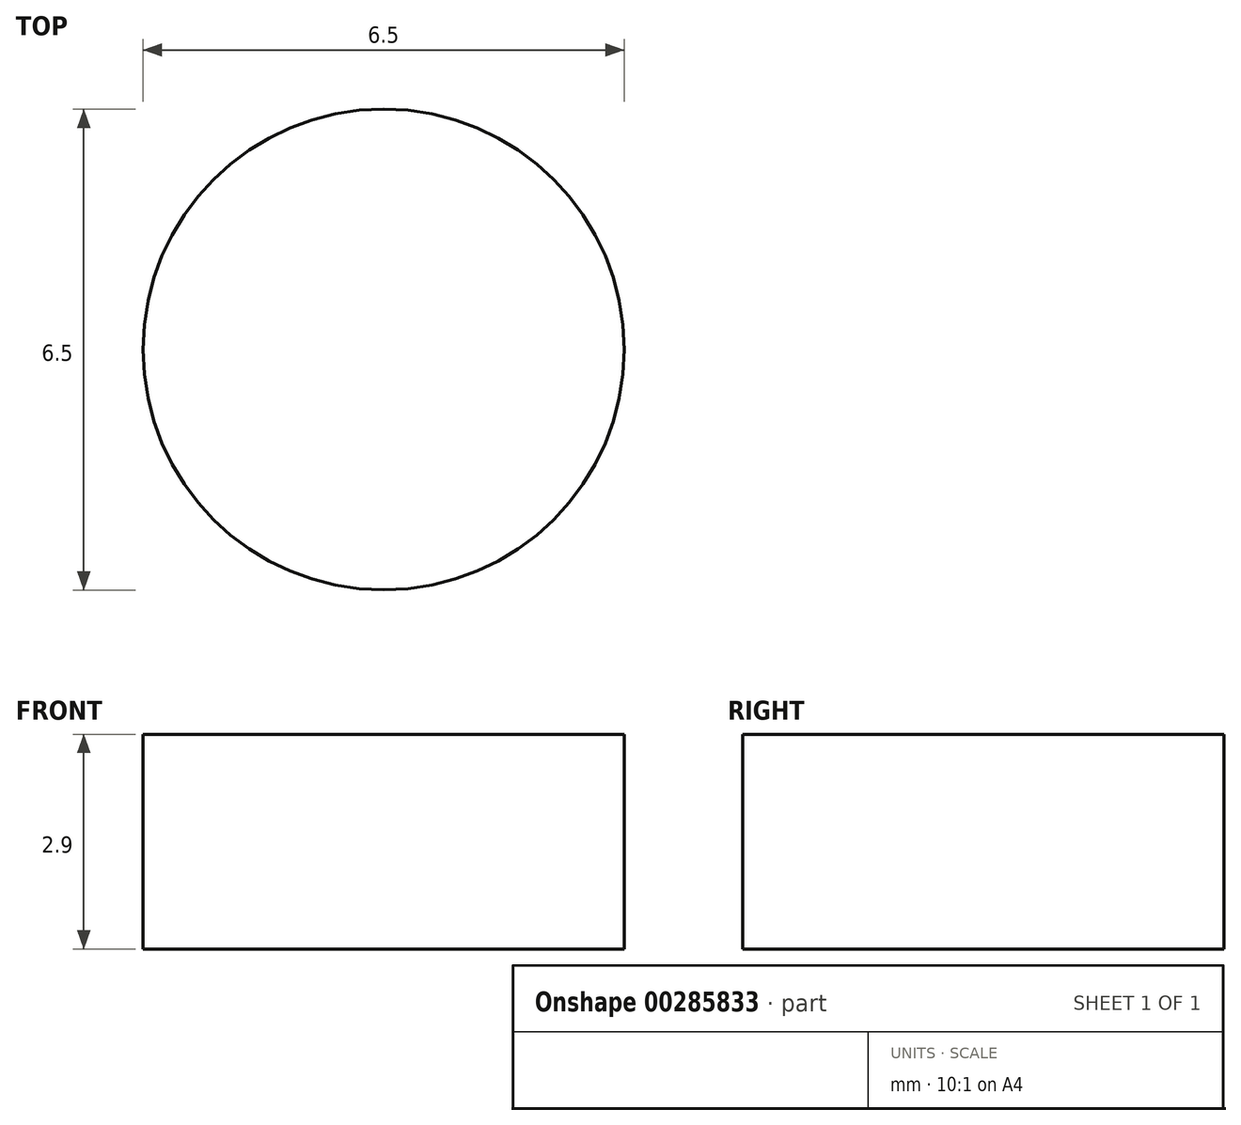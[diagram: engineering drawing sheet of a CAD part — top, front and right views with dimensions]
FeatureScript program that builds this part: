
annotation { "Feature Type Name" : "Feature", "Feature Type Description" : "" }
export const myFeature = defineFeature(function(context is Context, id is Id, definition is map)
    precondition{}
    {
        {
            var Q0;
            Q0=qCreatedBy(makeId("Top.planeOp"),FACE);
            var sketch = newSketch(context, id + "F0", { "sketchPlane" : qUnion([Q0])});
            skLineSegment(sketch, "E0", {"start": v(-29.75, -138) * mm, "end": v(-29.37, -138) * mm});
            skLineSegment(sketch, "E1", {"start": v(-29.37, -138) * mm, "end": v(-29.37, -133.46) * mm});
            skLineSegment(sketch, "E2", {"start": v(-29.37, -133.46) * mm, "end": v(-28.74, -138) * mm});
            skLineSegment(sketch, "E3", {"start": v(-28.74, -138) * mm, "end": v(-28.31, -138) * mm});
            skLineSegment(sketch, "E4", {"start": v(-28.31, -138) * mm, "end": v(-27.68, -133.46) * mm});
            skLineSegment(sketch, "E5", {"start": v(-27.68, -133.46) * mm, "end": v(-27.68, -138) * mm});
            skLineSegment(sketch, "E6", {"start": v(-27.68, -138) * mm, "end": v(-27.3, -138) * mm});
            skLineSegment(sketch, "E7", {"start": v(-27.3, -138) * mm, "end": v(-27.3, -133) * mm});
            skLineSegment(sketch, "E8", {"start": v(-27.3, -133) * mm, "end": v(-27.9, -133) * mm});
            skLineSegment(sketch, "E9", {"start": v(-27.9, -133) * mm, "end": v(-28.53, -137.4) * mm});
            skLineSegment(sketch, "E10", {"start": v(-28.53, -137.4) * mm, "end": v(-29.15, -133) * mm});
            skLineSegment(sketch, "E11", {"start": v(-29.15, -133) * mm, "end": v(-29.75, -133) * mm});
            skLineSegment(sketch, "E12", {"start": v(-29.75, -133) * mm, "end": v(-29.75, -138) * mm});
            skLineSegment(sketch, "E13", {"start": v(-24.53, -137.5) * mm, "end": v(-24.53, -137.51) * mm});
            skLineSegment(sketch, "E14", {"start": v(-24.53, -137.51) * mm, "end": v(-24.5, -137.76) * mm});
            skLineSegment(sketch, "E15", {"start": v(-24.5, -137.76) * mm, "end": v(-24.43, -137.93) * mm});
            skLineSegment(sketch, "E16", {"start": v(-24.43, -137.93) * mm, "end": v(-24.12, -138.07) * mm});
            skLineSegment(sketch, "E17", {"start": v(-24.12, -138.07) * mm, "end": v(-23.88, -138.01) * mm});
            skLineSegment(sketch, "E18", {"start": v(-23.88, -138.01) * mm, "end": v(-23.88, -137.52) * mm});
            skLineSegment(sketch, "E19", {"start": v(-23.88, -137.52) * mm, "end": v(-23.98, -137.54) * mm});
            skLineSegment(sketch, "E20", {"start": v(-23.98, -137.54) * mm, "end": v(-24.12, -137.45) * mm});
            skLineSegment(sketch, "E21", {"start": v(-24.12, -137.45) * mm, "end": v(-24.15, -137.16) * mm});
            skLineSegment(sketch, "E22", {"start": v(-24.15, -137.16) * mm, "end": v(-24.15, -135.16) * mm});
            skLineSegment(sketch, "E23", {"start": v(-24.15, -135.16) * mm, "end": v(-24.2, -134.65) * mm});
            skLineSegment(sketch, "E24", {"start": v(-24.2, -134.65) * mm, "end": v(-24.38, -134.29) * mm});
            skLineSegment(sketch, "E25", {"start": v(-24.38, -134.29) * mm, "end": v(-24.67, -134.07) * mm});
            skLineSegment(sketch, "E26", {"start": v(-24.67, -134.07) * mm, "end": v(-25.1, -133.99) * mm});
            skLineSegment(sketch, "E27", {"start": v(-25.1, -133.99) * mm, "end": v(-25.5, -134.08) * mm});
            skLineSegment(sketch, "E28", {"start": v(-25.5, -134.08) * mm, "end": v(-25.81, -134.32) * mm});
            skLineSegment(sketch, "E29", {"start": v(-25.81, -134.32) * mm, "end": v(-26, -134.7) * mm});
            skLineSegment(sketch, "E30", {"start": v(-26, -134.7) * mm, "end": v(-26.07, -135.2) * mm});
            skLineSegment(sketch, "E31", {"start": v(-26.07, -135.2) * mm, "end": v(-26.07, -135.25) * mm});
            skLineSegment(sketch, "E32", {"start": v(-26.07, -135.25) * mm, "end": v(-25.68, -135.25) * mm});
            skLineSegment(sketch, "E33", {"start": v(-25.68, -135.25) * mm, "end": v(-25.64, -134.95) * mm});
            skLineSegment(sketch, "E34", {"start": v(-25.64, -134.95) * mm, "end": v(-25.54, -134.73) * mm});
            skLineSegment(sketch, "E35", {"start": v(-25.54, -134.73) * mm, "end": v(-25.36, -134.6) * mm});
            skLineSegment(sketch, "E36", {"start": v(-25.36, -134.6) * mm, "end": v(-25.11, -134.55) * mm});
            skLineSegment(sketch, "E37", {"start": v(-25.11, -134.55) * mm, "end": v(-24.87, -134.59) * mm});
            skLineSegment(sketch, "E38", {"start": v(-24.87, -134.59) * mm, "end": v(-24.7, -134.7) * mm});
            skLineSegment(sketch, "E39", {"start": v(-24.7, -134.7) * mm, "end": v(-24.6, -134.88) * mm});
            skLineSegment(sketch, "E40", {"start": v(-24.6, -134.88) * mm, "end": v(-24.56, -135.14) * mm});
            skLineSegment(sketch, "E41", {"start": v(-24.56, -135.14) * mm, "end": v(-24.58, -135.45) * mm});
            skLineSegment(sketch, "E42", {"start": v(-24.58, -135.45) * mm, "end": v(-24.66, -135.6) * mm});
            skLineSegment(sketch, "E43", {"start": v(-24.66, -135.6) * mm, "end": v(-24.86, -135.67) * mm});
            skLineSegment(sketch, "E44", {"start": v(-24.86, -135.67) * mm, "end": v(-25.22, -135.73) * mm});
            skLineSegment(sketch, "E45", {"start": v(-25.22, -135.73) * mm, "end": v(-25.64, -135.86) * mm});
            skLineSegment(sketch, "E46", {"start": v(-25.64, -135.86) * mm, "end": v(-25.94, -136.09) * mm});
            skLineSegment(sketch, "E47", {"start": v(-25.94, -136.09) * mm, "end": v(-26.12, -136.45) * mm});
            skLineSegment(sketch, "E48", {"start": v(-26.12, -136.45) * mm, "end": v(-26.17, -136.98) * mm});
            skLineSegment(sketch, "E49", {"start": v(-26.17, -136.98) * mm, "end": v(-26.12, -137.46) * mm});
            skLineSegment(sketch, "E50", {"start": v(-26.12, -137.46) * mm, "end": v(-25.97, -137.8) * mm});
            skLineSegment(sketch, "E51", {"start": v(-25.97, -137.8) * mm, "end": v(-25.73, -138.03) * mm});
            skLineSegment(sketch, "E52", {"start": v(-25.73, -138.03) * mm, "end": v(-25.39, -138.11) * mm});
            skLineSegment(sketch, "E53", {"start": v(-25.39, -138.11) * mm, "end": v(-24.93, -137.96) * mm});
            skLineSegment(sketch, "E54", {"start": v(-24.93, -137.96) * mm, "end": v(-24.53, -137.5) * mm});
            skLineSegment(sketch, "E55", {"start": v(-24.58, -136.64) * mm, "end": v(-24.64, -137.02) * mm});
            skLineSegment(sketch, "E56", {"start": v(-24.64, -137.02) * mm, "end": v(-24.8, -137.3) * mm});
            skLineSegment(sketch, "E57", {"start": v(-24.8, -137.3) * mm, "end": v(-25.03, -137.5) * mm});
            skLineSegment(sketch, "E58", {"start": v(-25.03, -137.5) * mm, "end": v(-25.32, -137.56) * mm});
            skLineSegment(sketch, "E59", {"start": v(-25.32, -137.56) * mm, "end": v(-25.5, -137.52) * mm});
            skLineSegment(sketch, "E60", {"start": v(-25.5, -137.52) * mm, "end": v(-25.63, -137.4) * mm});
            skLineSegment(sketch, "E61", {"start": v(-25.63, -137.4) * mm, "end": v(-25.72, -137.2) * mm});
            skLineSegment(sketch, "E62", {"start": v(-25.72, -137.2) * mm, "end": v(-25.74, -136.92) * mm});
            skLineSegment(sketch, "E63", {"start": v(-25.74, -136.92) * mm, "end": v(-25.72, -136.67) * mm});
            skLineSegment(sketch, "E64", {"start": v(-25.72, -136.67) * mm, "end": v(-25.64, -136.49) * mm});
            skLineSegment(sketch, "E65", {"start": v(-25.64, -136.49) * mm, "end": v(-25.33, -136.29) * mm});
            skLineSegment(sketch, "E66", {"start": v(-25.33, -136.29) * mm, "end": v(-24.93, -136.2) * mm});
            skLineSegment(sketch, "E67", {"start": v(-24.93, -136.2) * mm, "end": v(-24.58, -136.03) * mm});
            skLineSegment(sketch, "E68", {"start": v(-24.58, -136.03) * mm, "end": v(-24.58, -136.64) * mm});
            skLineSegment(sketch, "E69", {"start": v(-22.61, -138) * mm, "end": v(-22.2, -138) * mm});
            skLineSegment(sketch, "E70", {"start": v(-22.2, -138) * mm, "end": v(-22.2, -134.4) * mm});
            skLineSegment(sketch, "E71", {"start": v(-22.2, -134.4) * mm, "end": v(-22.16, -133.92) * mm});
            skLineSegment(sketch, "E72", {"start": v(-22.16, -133.92) * mm, "end": v(-22.06, -133.57) * mm});
            skLineSegment(sketch, "E73", {"start": v(-22.06, -133.57) * mm, "end": v(-21.88, -133.37) * mm});
            skLineSegment(sketch, "E74", {"start": v(-21.88, -133.37) * mm, "end": v(-21.62, -133.3) * mm});
            skLineSegment(sketch, "E75", {"start": v(-21.62, -133.3) * mm, "end": v(-21.4, -133.36) * mm});
            skLineSegment(sketch, "E76", {"start": v(-21.4, -133.36) * mm, "end": v(-21.23, -133.52) * mm});
            skLineSegment(sketch, "E77", {"start": v(-21.23, -133.52) * mm, "end": v(-21.12, -133.77) * mm});
            skLineSegment(sketch, "E78", {"start": v(-21.12, -133.77) * mm, "end": v(-21.08, -134.1) * mm});
            skLineSegment(sketch, "E79", {"start": v(-21.08, -134.1) * mm, "end": v(-21.13, -134.47) * mm});
            skLineSegment(sketch, "E80", {"start": v(-21.13, -134.47) * mm, "end": v(-21.25, -134.72) * mm});
            skLineSegment(sketch, "E81", {"start": v(-21.25, -134.72) * mm, "end": v(-21.45, -134.88) * mm});
            skLineSegment(sketch, "E82", {"start": v(-21.45, -134.88) * mm, "end": v(-21.72, -134.93) * mm});
            skLineSegment(sketch, "E83", {"start": v(-21.72, -134.93) * mm, "end": v(-21.8, -134.93) * mm});
            skLineSegment(sketch, "E84", {"start": v(-21.8, -134.93) * mm, "end": v(-21.8, -135.45) * mm});
            skLineSegment(sketch, "E85", {"start": v(-21.8, -135.45) * mm, "end": v(-21.72, -135.45) * mm});
            skLineSegment(sketch, "E86", {"start": v(-21.72, -135.45) * mm, "end": v(-21.38, -135.52) * mm});
            skLineSegment(sketch, "E87", {"start": v(-21.38, -135.52) * mm, "end": v(-21.14, -135.7) * mm});
            skLineSegment(sketch, "E88", {"start": v(-21.14, -135.7) * mm, "end": v(-20.99, -136) * mm});
            skLineSegment(sketch, "E89", {"start": v(-20.99, -136) * mm, "end": v(-20.94, -136.43) * mm});
            skLineSegment(sketch, "E90", {"start": v(-20.94, -136.43) * mm, "end": v(-21, -136.9) * mm});
            skLineSegment(sketch, "E91", {"start": v(-21, -136.9) * mm, "end": v(-21.14, -137.23) * mm});
            skLineSegment(sketch, "E92", {"start": v(-21.14, -137.23) * mm, "end": v(-21.36, -137.45) * mm});
            skLineSegment(sketch, "E93", {"start": v(-21.36, -137.45) * mm, "end": v(-21.63, -137.52) * mm});
            skLineSegment(sketch, "E94", {"start": v(-21.63, -137.52) * mm, "end": v(-21.83, -137.48) * mm});
            skLineSegment(sketch, "E95", {"start": v(-21.83, -137.48) * mm, "end": v(-21.83, -138.07) * mm});
            skLineSegment(sketch, "E96", {"start": v(-21.83, -138.07) * mm, "end": v(-21.54, -138.12) * mm});
            skLineSegment(sketch, "E97", {"start": v(-21.54, -138.12) * mm, "end": v(-21.13, -138) * mm});
            skLineSegment(sketch, "E98", {"start": v(-21.13, -138) * mm, "end": v(-20.8, -137.64) * mm});
            skLineSegment(sketch, "E99", {"start": v(-20.8, -137.64) * mm, "end": v(-20.58, -137.09) * mm});
            skLineSegment(sketch, "E100", {"start": v(-20.58, -137.09) * mm, "end": v(-20.5, -136.36) * mm});
            skLineSegment(sketch, "E101", {"start": v(-20.5, -136.36) * mm, "end": v(-20.53, -135.94) * mm});
            skLineSegment(sketch, "E102", {"start": v(-20.53, -135.94) * mm, "end": v(-20.64, -135.57) * mm});
            skLineSegment(sketch, "E103", {"start": v(-20.64, -135.57) * mm, "end": v(-20.8, -135.29) * mm});
            skLineSegment(sketch, "E104", {"start": v(-20.8, -135.29) * mm, "end": v(-21.03, -135.1) * mm});
            skLineSegment(sketch, "E105", {"start": v(-21.03, -135.1) * mm, "end": v(-20.75, -134.71) * mm});
            skLineSegment(sketch, "E106", {"start": v(-20.75, -134.71) * mm, "end": v(-20.65, -134.05) * mm});
            skLineSegment(sketch, "E107", {"start": v(-20.65, -134.05) * mm, "end": v(-20.73, -133.52) * mm});
            skLineSegment(sketch, "E108", {"start": v(-20.73, -133.52) * mm, "end": v(-20.92, -133.1) * mm});
            skLineSegment(sketch, "E109", {"start": v(-20.92, -133.1) * mm, "end": v(-21.23, -132.84) * mm});
            skLineSegment(sketch, "E110", {"start": v(-21.23, -132.84) * mm, "end": v(-21.62, -132.74) * mm});
            skLineSegment(sketch, "E111", {"start": v(-21.62, -132.74) * mm, "end": v(-22.05, -132.84) * mm});
            skLineSegment(sketch, "E112", {"start": v(-22.05, -132.84) * mm, "end": v(-22.36, -133.14) * mm});
            skLineSegment(sketch, "E113", {"start": v(-22.36, -133.14) * mm, "end": v(-22.55, -133.63) * mm});
            skLineSegment(sketch, "E114", {"start": v(-22.55, -133.63) * mm, "end": v(-22.61, -134.3) * mm});
            skLineSegment(sketch, "E115", {"start": v(-22.61, -134.3) * mm, "end": v(-22.61, -138) * mm});
            skLineSegment(sketch, "E116", {"start": v(-17.9, -135.74) * mm, "end": v(-18.32, -135.6) * mm});
            skLineSegment(sketch, "E117", {"start": v(-18.32, -135.6) * mm, "end": v(-18.63, -135.43) * mm});
            skLineSegment(sketch, "E118", {"start": v(-18.63, -135.43) * mm, "end": v(-18.73, -135.1) * mm});
            skLineSegment(sketch, "E119", {"start": v(-18.73, -135.1) * mm, "end": v(-18.7, -134.85) * mm});
            skLineSegment(sketch, "E120", {"start": v(-18.7, -134.85) * mm, "end": v(-18.6, -134.68) * mm});
            skLineSegment(sketch, "E121", {"start": v(-18.6, -134.68) * mm, "end": v(-18.43, -134.57) * mm});
            skLineSegment(sketch, "E122", {"start": v(-18.43, -134.57) * mm, "end": v(-18.2, -134.53) * mm});
            skLineSegment(sketch, "E123", {"start": v(-18.2, -134.53) * mm, "end": v(-17.96, -134.57) * mm});
            skLineSegment(sketch, "E124", {"start": v(-17.96, -134.57) * mm, "end": v(-17.78, -134.7) * mm});
            skLineSegment(sketch, "E125", {"start": v(-17.78, -134.7) * mm, "end": v(-17.66, -134.9) * mm});
            skLineSegment(sketch, "E126", {"start": v(-17.66, -134.9) * mm, "end": v(-17.61, -135.16) * mm});
            skLineSegment(sketch, "E127", {"start": v(-17.61, -135.16) * mm, "end": v(-17.2, -135.16) * mm});
            skLineSegment(sketch, "E128", {"start": v(-17.2, -135.16) * mm, "end": v(-17.2, -135.14) * mm});
            skLineSegment(sketch, "E129", {"start": v(-17.2, -135.14) * mm, "end": v(-17.27, -134.67) * mm});
            skLineSegment(sketch, "E130", {"start": v(-17.27, -134.67) * mm, "end": v(-17.47, -134.3) * mm});
            skLineSegment(sketch, "E131", {"start": v(-17.47, -134.3) * mm, "end": v(-17.78, -134.08) * mm});
            skLineSegment(sketch, "E132", {"start": v(-17.78, -134.08) * mm, "end": v(-18.2, -133.99) * mm});
            skLineSegment(sketch, "E133", {"start": v(-18.2, -133.99) * mm, "end": v(-18.6, -134.08) * mm});
            skLineSegment(sketch, "E134", {"start": v(-18.6, -134.08) * mm, "end": v(-18.91, -134.31) * mm});
            skLineSegment(sketch, "E135", {"start": v(-18.91, -134.31) * mm, "end": v(-19.1, -134.67) * mm});
            skLineSegment(sketch, "E136", {"start": v(-19.1, -134.67) * mm, "end": v(-19.16, -135.11) * mm});
            skLineSegment(sketch, "E137", {"start": v(-19.16, -135.11) * mm, "end": v(-19.12, -135.55) * mm});
            skLineSegment(sketch, "E138", {"start": v(-19.12, -135.55) * mm, "end": v(-18.98, -135.85) * mm});
            skLineSegment(sketch, "E139", {"start": v(-18.98, -135.85) * mm, "end": v(-18.76, -136.06) * mm});
            skLineSegment(sketch, "E140", {"start": v(-18.76, -136.06) * mm, "end": v(-18.43, -136.22) * mm});
            skLineSegment(sketch, "E141", {"start": v(-18.43, -136.22) * mm, "end": v(-17.95, -136.39) * mm});
            skLineSegment(sketch, "E142", {"start": v(-17.95, -136.39) * mm, "end": v(-17.65, -136.57) * mm});
            skLineSegment(sketch, "E143", {"start": v(-17.65, -136.57) * mm, "end": v(-17.57, -136.71) * mm});
            skLineSegment(sketch, "E144", {"start": v(-17.57, -136.71) * mm, "end": v(-17.55, -136.93) * mm});
            skLineSegment(sketch, "E145", {"start": v(-17.55, -136.93) * mm, "end": v(-17.59, -137.2) * mm});
            skLineSegment(sketch, "E146", {"start": v(-17.59, -137.2) * mm, "end": v(-17.7, -137.4) * mm});
            skLineSegment(sketch, "E147", {"start": v(-17.7, -137.4) * mm, "end": v(-17.9, -137.53) * mm});
            skLineSegment(sketch, "E148", {"start": v(-17.9, -137.53) * mm, "end": v(-18.15, -137.57) * mm});
            skLineSegment(sketch, "E149", {"start": v(-18.15, -137.57) * mm, "end": v(-18.42, -137.53) * mm});
            skLineSegment(sketch, "E150", {"start": v(-18.42, -137.53) * mm, "end": v(-18.62, -137.38) * mm});
            skLineSegment(sketch, "E151", {"start": v(-18.62, -137.38) * mm, "end": v(-18.75, -137.13) * mm});
            skLineSegment(sketch, "E152", {"start": v(-18.75, -137.13) * mm, "end": v(-18.8, -136.8) * mm});
            skLineSegment(sketch, "E153", {"start": v(-18.8, -136.8) * mm, "end": v(-19.22, -136.8) * mm});
            skLineSegment(sketch, "E154", {"start": v(-19.22, -136.8) * mm, "end": v(-19.15, -137.37) * mm});
            skLineSegment(sketch, "E155", {"start": v(-19.15, -137.37) * mm, "end": v(-18.95, -137.79) * mm});
            skLineSegment(sketch, "E156", {"start": v(-18.95, -137.79) * mm, "end": v(-18.63, -138.04) * mm});
            skLineSegment(sketch, "E157", {"start": v(-18.63, -138.04) * mm, "end": v(-18.2, -138.13) * mm});
            skLineSegment(sketch, "E158", {"start": v(-18.2, -138.13) * mm, "end": v(-17.73, -138.04) * mm});
            skLineSegment(sketch, "E159", {"start": v(-17.73, -138.04) * mm, "end": v(-17.4, -137.79) * mm});
            skLineSegment(sketch, "E160", {"start": v(-17.4, -137.79) * mm, "end": v(-17.19, -137.38) * mm});
            skLineSegment(sketch, "E161", {"start": v(-17.19, -137.38) * mm, "end": v(-17.11, -136.86) * mm});
            skLineSegment(sketch, "E162", {"start": v(-17.11, -136.86) * mm, "end": v(-17.17, -136.4) * mm});
            skLineSegment(sketch, "E163", {"start": v(-17.17, -136.4) * mm, "end": v(-17.32, -136.1) * mm});
            skLineSegment(sketch, "E164", {"start": v(-17.32, -136.1) * mm, "end": v(-17.57, -135.9) * mm});
            skLineSegment(sketch, "E165", {"start": v(-17.57, -135.9) * mm, "end": v(-17.9, -135.74) * mm});
            skLineSegment(sketch, "E166", {"start": v(-15.16, -134.8) * mm, "end": v(-15.16, -136.73) * mm});
            skLineSegment(sketch, "E167", {"start": v(-15.16, -136.73) * mm, "end": v(-15.13, -137.36) * mm});
            skLineSegment(sketch, "E168", {"start": v(-15.13, -137.36) * mm, "end": v(-15, -137.8) * mm});
            skLineSegment(sketch, "E169", {"start": v(-15, -137.8) * mm, "end": v(-14.72, -138.05) * mm});
            skLineSegment(sketch, "E170", {"start": v(-14.72, -138.05) * mm, "end": v(-14.26, -138.13) * mm});
            skLineSegment(sketch, "E171", {"start": v(-14.26, -138.13) * mm, "end": v(-13.75, -138.1) * mm});
            skLineSegment(sketch, "E172", {"start": v(-13.75, -138.1) * mm, "end": v(-13.75, -137.55) * mm});
            skLineSegment(sketch, "E173", {"start": v(-13.75, -137.55) * mm, "end": v(-14.12, -137.6) * mm});
            skLineSegment(sketch, "E174", {"start": v(-14.12, -137.6) * mm, "end": v(-14.46, -137.53) * mm});
            skLineSegment(sketch, "E175", {"start": v(-14.46, -137.53) * mm, "end": v(-14.64, -137.35) * mm});
            skLineSegment(sketch, "E176", {"start": v(-14.64, -137.35) * mm, "end": v(-14.72, -137.05) * mm});
            skLineSegment(sketch, "E177", {"start": v(-14.72, -137.05) * mm, "end": v(-14.73, -136.63) * mm});
            skLineSegment(sketch, "E178", {"start": v(-14.73, -136.63) * mm, "end": v(-14.73, -134.8) * mm});
            skLineSegment(sketch, "E179", {"start": v(-14.73, -134.8) * mm, "end": v(-13.75, -134.8) * mm});
            skLineSegment(sketch, "E180", {"start": v(-13.75, -134.8) * mm, "end": v(-13.75, -134.26) * mm});
            skLineSegment(sketch, "E181", {"start": v(-13.75, -134.26) * mm, "end": v(-14.73, -134.26) * mm});
            skLineSegment(sketch, "E182", {"start": v(-14.73, -134.26) * mm, "end": v(-14.73, -133.13) * mm});
            skLineSegment(sketch, "E183", {"start": v(-14.73, -133.13) * mm, "end": v(-15.16, -133.13) * mm});
            skLineSegment(sketch, "E184", {"start": v(-15.16, -133.13) * mm, "end": v(-15.16, -134.26) * mm});
            skLineSegment(sketch, "E185", {"start": v(-15.16, -134.26) * mm, "end": v(-15.9, -134.26) * mm});
            skLineSegment(sketch, "E186", {"start": v(-15.9, -134.26) * mm, "end": v(-15.9, -134.8) * mm});
            skLineSegment(sketch, "E187", {"start": v(-15.9, -134.8) * mm, "end": v(-15.16, -134.8) * mm});
            skLineSegment(sketch, "E188", {"start": v(-10.73, -137.5) * mm, "end": v(-10.73, -137.51) * mm});
            skLineSegment(sketch, "E189", {"start": v(-10.73, -137.51) * mm, "end": v(-10.7, -137.76) * mm});
            skLineSegment(sketch, "E190", {"start": v(-10.7, -137.76) * mm, "end": v(-10.63, -137.93) * mm});
            skLineSegment(sketch, "E191", {"start": v(-10.63, -137.93) * mm, "end": v(-10.32, -138.07) * mm});
            skLineSegment(sketch, "E192", {"start": v(-10.32, -138.07) * mm, "end": v(-10.08, -138.01) * mm});
            skLineSegment(sketch, "E193", {"start": v(-10.08, -138.01) * mm, "end": v(-10.08, -137.52) * mm});
            skLineSegment(sketch, "E194", {"start": v(-10.08, -137.52) * mm, "end": v(-10.19, -137.54) * mm});
            skLineSegment(sketch, "E195", {"start": v(-10.19, -137.54) * mm, "end": v(-10.32, -137.45) * mm});
            skLineSegment(sketch, "E196", {"start": v(-10.32, -137.45) * mm, "end": v(-10.35, -137.16) * mm});
            skLineSegment(sketch, "E197", {"start": v(-10.35, -137.16) * mm, "end": v(-10.35, -135.16) * mm});
            skLineSegment(sketch, "E198", {"start": v(-10.35, -135.16) * mm, "end": v(-10.4, -134.65) * mm});
            skLineSegment(sketch, "E199", {"start": v(-10.4, -134.65) * mm, "end": v(-10.58, -134.29) * mm});
            skLineSegment(sketch, "E200", {"start": v(-10.58, -134.29) * mm, "end": v(-10.88, -134.07) * mm});
            skLineSegment(sketch, "E201", {"start": v(-10.88, -134.07) * mm, "end": v(-11.3, -133.99) * mm});
            skLineSegment(sketch, "E202", {"start": v(-11.3, -133.99) * mm, "end": v(-11.71, -134.08) * mm});
            skLineSegment(sketch, "E203", {"start": v(-11.71, -134.08) * mm, "end": v(-12.01, -134.32) * mm});
            skLineSegment(sketch, "E204", {"start": v(-12.01, -134.32) * mm, "end": v(-12.2, -134.7) * mm});
            skLineSegment(sketch, "E205", {"start": v(-12.2, -134.7) * mm, "end": v(-12.27, -135.2) * mm});
            skLineSegment(sketch, "E206", {"start": v(-12.27, -135.2) * mm, "end": v(-12.27, -135.25) * mm});
            skLineSegment(sketch, "E207", {"start": v(-12.27, -135.25) * mm, "end": v(-11.88, -135.25) * mm});
            skLineSegment(sketch, "E208", {"start": v(-11.88, -135.25) * mm, "end": v(-11.85, -134.95) * mm});
            skLineSegment(sketch, "E209", {"start": v(-11.85, -134.95) * mm, "end": v(-11.74, -134.73) * mm});
            skLineSegment(sketch, "E210", {"start": v(-11.74, -134.73) * mm, "end": v(-11.56, -134.6) * mm});
            skLineSegment(sketch, "E211", {"start": v(-11.56, -134.6) * mm, "end": v(-11.31, -134.55) * mm});
            skLineSegment(sketch, "E212", {"start": v(-11.31, -134.55) * mm, "end": v(-11.07, -134.59) * mm});
            skLineSegment(sketch, "E213", {"start": v(-11.07, -134.59) * mm, "end": v(-10.9, -134.7) * mm});
            skLineSegment(sketch, "E214", {"start": v(-10.9, -134.7) * mm, "end": v(-10.8, -134.88) * mm});
            skLineSegment(sketch, "E215", {"start": v(-10.8, -134.88) * mm, "end": v(-10.76, -135.14) * mm});
            skLineSegment(sketch, "E216", {"start": v(-10.76, -135.14) * mm, "end": v(-10.78, -135.45) * mm});
            skLineSegment(sketch, "E217", {"start": v(-10.78, -135.45) * mm, "end": v(-10.86, -135.6) * mm});
            skLineSegment(sketch, "E218", {"start": v(-10.86, -135.6) * mm, "end": v(-11.06, -135.67) * mm});
            skLineSegment(sketch, "E219", {"start": v(-11.06, -135.67) * mm, "end": v(-11.43, -135.73) * mm});
            skLineSegment(sketch, "E220", {"start": v(-11.43, -135.73) * mm, "end": v(-11.85, -135.86) * mm});
            skLineSegment(sketch, "E221", {"start": v(-11.85, -135.86) * mm, "end": v(-12.15, -136.09) * mm});
            skLineSegment(sketch, "E222", {"start": v(-12.15, -136.09) * mm, "end": v(-12.32, -136.45) * mm});
            skLineSegment(sketch, "E223", {"start": v(-12.32, -136.45) * mm, "end": v(-12.38, -136.98) * mm});
            skLineSegment(sketch, "E224", {"start": v(-12.38, -136.98) * mm, "end": v(-12.33, -137.46) * mm});
            skLineSegment(sketch, "E225", {"start": v(-12.33, -137.46) * mm, "end": v(-12.18, -137.8) * mm});
            skLineSegment(sketch, "E226", {"start": v(-12.18, -137.8) * mm, "end": v(-11.93, -138.03) * mm});
            skLineSegment(sketch, "E227", {"start": v(-11.93, -138.03) * mm, "end": v(-11.6, -138.11) * mm});
            skLineSegment(sketch, "E228", {"start": v(-11.6, -138.11) * mm, "end": v(-11.14, -137.96) * mm});
            skLineSegment(sketch, "E229", {"start": v(-11.14, -137.96) * mm, "end": v(-10.73, -137.5) * mm});
            skLineSegment(sketch, "E230", {"start": v(-10.78, -136.64) * mm, "end": v(-10.84, -137.02) * mm});
            skLineSegment(sketch, "E231", {"start": v(-10.84, -137.02) * mm, "end": v(-11, -137.3) * mm});
            skLineSegment(sketch, "E232", {"start": v(-11, -137.3) * mm, "end": v(-11.23, -137.5) * mm});
            skLineSegment(sketch, "E233", {"start": v(-11.23, -137.5) * mm, "end": v(-11.52, -137.56) * mm});
            skLineSegment(sketch, "E234", {"start": v(-11.52, -137.56) * mm, "end": v(-11.7, -137.52) * mm});
            skLineSegment(sketch, "E235", {"start": v(-11.7, -137.52) * mm, "end": v(-11.84, -137.4) * mm});
            skLineSegment(sketch, "E236", {"start": v(-11.84, -137.4) * mm, "end": v(-11.92, -137.2) * mm});
            skLineSegment(sketch, "E237", {"start": v(-11.92, -137.2) * mm, "end": v(-11.95, -136.92) * mm});
            skLineSegment(sketch, "E238", {"start": v(-11.95, -136.92) * mm, "end": v(-11.93, -136.67) * mm});
            skLineSegment(sketch, "E239", {"start": v(-11.93, -136.67) * mm, "end": v(-11.85, -136.49) * mm});
            skLineSegment(sketch, "E240", {"start": v(-11.85, -136.49) * mm, "end": v(-11.53, -136.29) * mm});
            skLineSegment(sketch, "E241", {"start": v(-11.53, -136.29) * mm, "end": v(-11.14, -136.2) * mm});
            skLineSegment(sketch, "E242", {"start": v(-11.14, -136.2) * mm, "end": v(-10.78, -136.03) * mm});
            skLineSegment(sketch, "E243", {"start": v(-10.78, -136.03) * mm, "end": v(-10.78, -136.64) * mm});
            skLineSegment(sketch, "E244", {"start": v(-8.44, -137.4) * mm, "end": v(-8.12, -137.95) * mm});
            skLineSegment(sketch, "E245", {"start": v(-8.12, -137.95) * mm, "end": v(-7.68, -138.13) * mm});
            skLineSegment(sketch, "E246", {"start": v(-7.68, -138.13) * mm, "end": v(-7.27, -138) * mm});
            skLineSegment(sketch, "E247", {"start": v(-7.27, -138) * mm, "end": v(-6.94, -137.59) * mm});
            skLineSegment(sketch, "E248", {"start": v(-6.94, -137.59) * mm, "end": v(-6.74, -136.93) * mm});
            skLineSegment(sketch, "E249", {"start": v(-6.74, -136.93) * mm, "end": v(-6.66, -136.06) * mm});
            skLineSegment(sketch, "E250", {"start": v(-6.66, -136.06) * mm, "end": v(-6.74, -135.19) * mm});
            skLineSegment(sketch, "E251", {"start": v(-6.74, -135.19) * mm, "end": v(-6.95, -134.54) * mm});
            skLineSegment(sketch, "E252", {"start": v(-6.95, -134.54) * mm, "end": v(-7.27, -134.13) * mm});
            skLineSegment(sketch, "E253", {"start": v(-7.27, -134.13) * mm, "end": v(-7.68, -133.99) * mm});
            skLineSegment(sketch, "E254", {"start": v(-7.68, -133.99) * mm, "end": v(-8.11, -134.18) * mm});
            skLineSegment(sketch, "E255", {"start": v(-8.11, -134.18) * mm, "end": v(-8.3, -134.4) * mm});
            skLineSegment(sketch, "E256", {"start": v(-8.3, -134.4) * mm, "end": v(-8.44, -134.72) * mm});
            skLineSegment(sketch, "E257", {"start": v(-8.44, -134.72) * mm, "end": v(-8.44, -132.82) * mm});
            skLineSegment(sketch, "E258", {"start": v(-8.44, -132.82) * mm, "end": v(-8.87, -132.82) * mm});
            skLineSegment(sketch, "E259", {"start": v(-8.87, -132.82) * mm, "end": v(-8.87, -138) * mm});
            skLineSegment(sketch, "E260", {"start": v(-8.87, -138) * mm, "end": v(-8.44, -138) * mm});
            skLineSegment(sketch, "E261", {"start": v(-8.44, -138) * mm, "end": v(-8.44, -137.4) * mm});
            skLineSegment(sketch, "E262", {"start": v(-7.1, -136.06) * mm, "end": v(-7.15, -136.7) * mm});
            skLineSegment(sketch, "E263", {"start": v(-7.15, -136.7) * mm, "end": v(-7.28, -137.18) * mm});
            skLineSegment(sketch, "E264", {"start": v(-7.28, -137.18) * mm, "end": v(-7.5, -137.47) * mm});
            skLineSegment(sketch, "E265", {"start": v(-7.5, -137.47) * mm, "end": v(-7.76, -137.56) * mm});
            skLineSegment(sketch, "E266", {"start": v(-7.76, -137.56) * mm, "end": v(-8.05, -137.47) * mm});
            skLineSegment(sketch, "E267", {"start": v(-8.05, -137.47) * mm, "end": v(-8.26, -137.18) * mm});
            skLineSegment(sketch, "E268", {"start": v(-8.26, -137.18) * mm, "end": v(-8.39, -136.71) * mm});
            skLineSegment(sketch, "E269", {"start": v(-8.39, -136.71) * mm, "end": v(-8.43, -136.06) * mm});
            skLineSegment(sketch, "E270", {"start": v(-8.43, -136.06) * mm, "end": v(-8.39, -135.4) * mm});
            skLineSegment(sketch, "E271", {"start": v(-8.39, -135.4) * mm, "end": v(-8.26, -134.94) * mm});
            skLineSegment(sketch, "E272", {"start": v(-8.26, -134.94) * mm, "end": v(-8.05, -134.66) * mm});
            skLineSegment(sketch, "E273", {"start": v(-8.05, -134.66) * mm, "end": v(-7.76, -134.56) * mm});
            skLineSegment(sketch, "E274", {"start": v(-7.76, -134.56) * mm, "end": v(-7.5, -134.66) * mm});
            skLineSegment(sketch, "E275", {"start": v(-7.5, -134.66) * mm, "end": v(-7.28, -134.95) * mm});
            skLineSegment(sketch, "E276", {"start": v(-7.28, -134.95) * mm, "end": v(-7.15, -135.42) * mm});
            skLineSegment(sketch, "E277", {"start": v(-7.15, -135.42) * mm, "end": v(-7.1, -136.06) * mm});
            skLineSegment(sketch, "E278", {"start": v(-4.72, -138) * mm, "end": v(-4.04, -138) * mm});
            skLineSegment(sketch, "E279", {"start": v(-4.04, -138) * mm, "end": v(-4.04, -136.92) * mm});
            skLineSegment(sketch, "E280", {"start": v(-4.04, -136.92) * mm, "end": v(-4.72, -136.92) * mm});
            skLineSegment(sketch, "E281", {"start": v(-4.72, -136.92) * mm, "end": v(-4.72, -138) * mm});
            skLineSegment(sketch, "E282", {"start": v(-4.72, -135.2) * mm, "end": v(-4.04, -135.2) * mm});
            skLineSegment(sketch, "E283", {"start": v(-4.04, -135.2) * mm, "end": v(-4.04, -134.13) * mm});
            skLineSegment(sketch, "E284", {"start": v(-4.04, -134.13) * mm, "end": v(-4.72, -134.13) * mm});
            skLineSegment(sketch, "E285", {"start": v(-4.72, -134.13) * mm, "end": v(-4.72, -135.2) * mm});
            skLineSegment(sketch, "E286", {"start": v(5.88, -138) * mm, "end": v(6.33, -138) * mm});
            skLineSegment(sketch, "E287", {"start": v(6.33, -138) * mm, "end": v(6.33, -132.96) * mm});
            skLineSegment(sketch, "E288", {"start": v(6.33, -132.96) * mm, "end": v(6, -132.96) * mm});
            skLineSegment(sketch, "E289", {"start": v(6, -132.96) * mm, "end": v(5.9, -133.4) * mm});
            skLineSegment(sketch, "E290", {"start": v(5.9, -133.4) * mm, "end": v(5.73, -133.7) * mm});
            skLineSegment(sketch, "E291", {"start": v(5.73, -133.7) * mm, "end": v(5.46, -133.87) * mm});
            skLineSegment(sketch, "E292", {"start": v(5.46, -133.87) * mm, "end": v(5.09, -133.93) * mm});
            skLineSegment(sketch, "E293", {"start": v(5.09, -133.93) * mm, "end": v(5.09, -134.44) * mm});
            skLineSegment(sketch, "E294", {"start": v(5.09, -134.44) * mm, "end": v(5.88, -134.44) * mm});
            skLineSegment(sketch, "E295", {"start": v(5.88, -134.44) * mm, "end": v(5.88, -138) * mm});
            skLineSegment(sketch, "E296", {"start": v(9.08, -138) * mm, "end": v(9.75, -138) * mm});
            skLineSegment(sketch, "E297", {"start": v(9.75, -138) * mm, "end": v(9.75, -136.92) * mm});
            skLineSegment(sketch, "E298", {"start": v(9.75, -136.92) * mm, "end": v(9.08, -136.92) * mm});
            skLineSegment(sketch, "E299", {"start": v(9.08, -136.92) * mm, "end": v(9.08, -138) * mm});
            skLineSegment(sketch, "E300", {"start": v(9.08, -135.2) * mm, "end": v(9.75, -135.2) * mm});
            skLineSegment(sketch, "E301", {"start": v(9.75, -135.2) * mm, "end": v(9.75, -134.13) * mm});
            skLineSegment(sketch, "E302", {"start": v(9.75, -134.13) * mm, "end": v(9.08, -134.13) * mm});
            skLineSegment(sketch, "E303", {"start": v(9.08, -134.13) * mm, "end": v(9.08, -135.2) * mm});
            skLineSegment(sketch, "E304", {"start": v(12.78, -138) * mm, "end": v(13.22, -138) * mm});
            skLineSegment(sketch, "E305", {"start": v(13.22, -138) * mm, "end": v(13.22, -132.96) * mm});
            skLineSegment(sketch, "E306", {"start": v(13.22, -132.96) * mm, "end": v(12.9, -132.96) * mm});
            skLineSegment(sketch, "E307", {"start": v(12.9, -132.96) * mm, "end": v(12.8, -133.4) * mm});
            skLineSegment(sketch, "E308", {"start": v(12.8, -133.4) * mm, "end": v(12.63, -133.7) * mm});
            skLineSegment(sketch, "E309", {"start": v(12.63, -133.7) * mm, "end": v(12.36, -133.87) * mm});
            skLineSegment(sketch, "E310", {"start": v(12.36, -133.87) * mm, "end": v(11.98, -133.93) * mm});
            skLineSegment(sketch, "E311", {"start": v(11.98, -133.93) * mm, "end": v(11.98, -134.44) * mm});
            skLineSegment(sketch, "E312", {"start": v(11.98, -134.44) * mm, "end": v(12.78, -134.44) * mm});
            skLineSegment(sketch, "E313", {"start": v(12.78, -134.44) * mm, "end": v(12.78, -138) * mm});
            skLineSegment(sketch, "E314", {"start": v(-28.25, -144.38) * mm, "end": v(-28.67, -144.23) * mm});
            skLineSegment(sketch, "E315", {"start": v(-28.67, -144.23) * mm, "end": v(-28.98, -144.07) * mm});
            skLineSegment(sketch, "E316", {"start": v(-28.98, -144.07) * mm, "end": v(-29.08, -143.73) * mm});
            skLineSegment(sketch, "E317", {"start": v(-29.08, -143.73) * mm, "end": v(-29.05, -143.5) * mm});
            skLineSegment(sketch, "E318", {"start": v(-29.05, -143.5) * mm, "end": v(-28.95, -143.32) * mm});
            skLineSegment(sketch, "E319", {"start": v(-28.95, -143.32) * mm, "end": v(-28.78, -143.21) * mm});
            skLineSegment(sketch, "E320", {"start": v(-28.78, -143.21) * mm, "end": v(-28.54, -143.17) * mm});
            skLineSegment(sketch, "E321", {"start": v(-28.54, -143.17) * mm, "end": v(-28.3, -143.21) * mm});
            skLineSegment(sketch, "E322", {"start": v(-28.3, -143.21) * mm, "end": v(-28.13, -143.34) * mm});
            skLineSegment(sketch, "E323", {"start": v(-28.13, -143.34) * mm, "end": v(-28.01, -143.54) * mm});
            skLineSegment(sketch, "E324", {"start": v(-28.01, -143.54) * mm, "end": v(-27.96, -143.8) * mm});
            skLineSegment(sketch, "E325", {"start": v(-27.96, -143.8) * mm, "end": v(-27.54, -143.8) * mm});
            skLineSegment(sketch, "E326", {"start": v(-27.54, -143.8) * mm, "end": v(-27.54, -143.78) * mm});
            skLineSegment(sketch, "E327", {"start": v(-27.54, -143.78) * mm, "end": v(-27.61, -143.31) * mm});
            skLineSegment(sketch, "E328", {"start": v(-27.61, -143.31) * mm, "end": v(-27.81, -142.95) * mm});
            skLineSegment(sketch, "E329", {"start": v(-27.81, -142.95) * mm, "end": v(-28.13, -142.71) * mm});
            skLineSegment(sketch, "E330", {"start": v(-28.13, -142.71) * mm, "end": v(-28.54, -142.63) * mm});
            skLineSegment(sketch, "E331", {"start": v(-28.54, -142.63) * mm, "end": v(-28.96, -142.71) * mm});
            skLineSegment(sketch, "E332", {"start": v(-28.96, -142.71) * mm, "end": v(-29.26, -142.95) * mm});
            skLineSegment(sketch, "E333", {"start": v(-29.26, -142.95) * mm, "end": v(-29.45, -143.3) * mm});
            skLineSegment(sketch, "E334", {"start": v(-29.45, -143.3) * mm, "end": v(-29.51, -143.75) * mm});
            skLineSegment(sketch, "E335", {"start": v(-29.51, -143.75) * mm, "end": v(-29.47, -144.18) * mm});
            skLineSegment(sketch, "E336", {"start": v(-29.47, -144.18) * mm, "end": v(-29.33, -144.49) * mm});
            skLineSegment(sketch, "E337", {"start": v(-29.33, -144.49) * mm, "end": v(-29.1, -144.7) * mm});
            skLineSegment(sketch, "E338", {"start": v(-29.1, -144.7) * mm, "end": v(-28.78, -144.85) * mm});
            skLineSegment(sketch, "E339", {"start": v(-28.78, -144.85) * mm, "end": v(-28.3, -145.03) * mm});
            skLineSegment(sketch, "E340", {"start": v(-28.3, -145.03) * mm, "end": v(-28, -145.2) * mm});
            skLineSegment(sketch, "E341", {"start": v(-28, -145.2) * mm, "end": v(-27.92, -145.35) * mm});
            skLineSegment(sketch, "E342", {"start": v(-27.92, -145.35) * mm, "end": v(-27.9, -145.57) * mm});
            skLineSegment(sketch, "E343", {"start": v(-27.9, -145.57) * mm, "end": v(-27.94, -145.83) * mm});
            skLineSegment(sketch, "E344", {"start": v(-27.94, -145.83) * mm, "end": v(-28.06, -146.04) * mm});
            skLineSegment(sketch, "E345", {"start": v(-28.06, -146.04) * mm, "end": v(-28.25, -146.17) * mm});
            skLineSegment(sketch, "E346", {"start": v(-28.25, -146.17) * mm, "end": v(-28.5, -146.2) * mm});
            skLineSegment(sketch, "E347", {"start": v(-28.5, -146.2) * mm, "end": v(-28.77, -146.17) * mm});
            skLineSegment(sketch, "E348", {"start": v(-28.77, -146.17) * mm, "end": v(-28.97, -146.01) * mm});
            skLineSegment(sketch, "E349", {"start": v(-28.97, -146.01) * mm, "end": v(-29.1, -145.77) * mm});
            skLineSegment(sketch, "E350", {"start": v(-29.1, -145.77) * mm, "end": v(-29.15, -145.43) * mm});
            skLineSegment(sketch, "E351", {"start": v(-29.15, -145.43) * mm, "end": v(-29.57, -145.43) * mm});
            skLineSegment(sketch, "E352", {"start": v(-29.57, -145.43) * mm, "end": v(-29.5, -146) * mm});
            skLineSegment(sketch, "E353", {"start": v(-29.5, -146) * mm, "end": v(-29.3, -146.43) * mm});
            skLineSegment(sketch, "E354", {"start": v(-29.3, -146.43) * mm, "end": v(-28.98, -146.68) * mm});
            skLineSegment(sketch, "E355", {"start": v(-28.98, -146.68) * mm, "end": v(-28.54, -146.77) * mm});
            skLineSegment(sketch, "E356", {"start": v(-28.54, -146.77) * mm, "end": v(-28.08, -146.68) * mm});
            skLineSegment(sketch, "E357", {"start": v(-28.08, -146.68) * mm, "end": v(-27.74, -146.43) * mm});
            skLineSegment(sketch, "E358", {"start": v(-27.74, -146.43) * mm, "end": v(-27.54, -146.02) * mm});
            skLineSegment(sketch, "E359", {"start": v(-27.54, -146.02) * mm, "end": v(-27.46, -145.5) * mm});
            skLineSegment(sketch, "E360", {"start": v(-27.46, -145.5) * mm, "end": v(-27.52, -145.04) * mm});
            skLineSegment(sketch, "E361", {"start": v(-27.52, -145.04) * mm, "end": v(-27.67, -144.73) * mm});
            skLineSegment(sketch, "E362", {"start": v(-27.67, -144.73) * mm, "end": v(-27.92, -144.53) * mm});
            skLineSegment(sketch, "E363", {"start": v(-27.92, -144.53) * mm, "end": v(-28.25, -144.38) * mm});
            skLineSegment(sketch, "E364", {"start": v(-22.77, -144.53) * mm, "end": v(-22.77, -145.02) * mm});
            skLineSegment(sketch, "E365", {"start": v(-22.77, -145.02) * mm, "end": v(-20.5, -145.02) * mm});
            skLineSegment(sketch, "E366", {"start": v(-20.5, -145.02) * mm, "end": v(-20.5, -144.53) * mm});
            skLineSegment(sketch, "E367", {"start": v(-20.5, -144.53) * mm, "end": v(-22.77, -144.53) * mm});
            skLineSegment(sketch, "E368", {"start": v(-22.77, -143.13) * mm, "end": v(-22.77, -143.63) * mm});
            skLineSegment(sketch, "E369", {"start": v(-22.77, -143.63) * mm, "end": v(-20.5, -143.63) * mm});
            skLineSegment(sketch, "E370", {"start": v(-20.5, -143.63) * mm, "end": v(-20.5, -143.13) * mm});
            skLineSegment(sketch, "E371", {"start": v(-20.5, -143.13) * mm, "end": v(-22.77, -143.13) * mm});
            skLineSegment(sketch, "E372", {"start": v(-15.96, -145.06) * mm, "end": v(-15.96, -145.11) * mm});
            skLineSegment(sketch, "E373", {"start": v(-15.96, -145.11) * mm, "end": v(-15.88, -145.8) * mm});
            skLineSegment(sketch, "E374", {"start": v(-15.88, -145.8) * mm, "end": v(-15.65, -146.32) * mm});
            skLineSegment(sketch, "E375", {"start": v(-15.65, -146.32) * mm, "end": v(-15.3, -146.66) * mm});
            skLineSegment(sketch, "E376", {"start": v(-15.3, -146.66) * mm, "end": v(-14.81, -146.78) * mm});
            skLineSegment(sketch, "E377", {"start": v(-14.81, -146.78) * mm, "end": v(-14.3, -146.66) * mm});
            skLineSegment(sketch, "E378", {"start": v(-14.3, -146.66) * mm, "end": v(-13.92, -146.34) * mm});
            skLineSegment(sketch, "E379", {"start": v(-13.92, -146.34) * mm, "end": v(-13.67, -145.83) * mm});
            skLineSegment(sketch, "E380", {"start": v(-13.67, -145.83) * mm, "end": v(-13.59, -145.19) * mm});
            skLineSegment(sketch, "E381", {"start": v(-13.59, -145.19) * mm, "end": v(-13.63, -144.76) * mm});
            skLineSegment(sketch, "E382", {"start": v(-13.63, -144.76) * mm, "end": v(-13.73, -144.41) * mm});
            skLineSegment(sketch, "E383", {"start": v(-13.73, -144.41) * mm, "end": v(-13.91, -144.15) * mm});
            skLineSegment(sketch, "E384", {"start": v(-13.91, -144.15) * mm, "end": v(-14.15, -143.95) * mm});
            skLineSegment(sketch, "E385", {"start": v(-14.15, -143.95) * mm, "end": v(-13.83, -143.56) * mm});
            skLineSegment(sketch, "E386", {"start": v(-13.83, -143.56) * mm, "end": v(-13.71, -142.95) * mm});
            skLineSegment(sketch, "E387", {"start": v(-13.71, -142.95) * mm, "end": v(-13.79, -142.38) * mm});
            skLineSegment(sketch, "E388", {"start": v(-13.79, -142.38) * mm, "end": v(-14, -141.96) * mm});
            skLineSegment(sketch, "E389", {"start": v(-14, -141.96) * mm, "end": v(-14.34, -141.7) * mm});
            skLineSegment(sketch, "E390", {"start": v(-14.34, -141.7) * mm, "end": v(-14.81, -141.6) * mm});
            skLineSegment(sketch, "E391", {"start": v(-14.81, -141.6) * mm, "end": v(-15.25, -141.71) * mm});
            skLineSegment(sketch, "E392", {"start": v(-15.25, -141.71) * mm, "end": v(-15.6, -142.03) * mm});
            skLineSegment(sketch, "E393", {"start": v(-15.6, -142.03) * mm, "end": v(-15.81, -142.53) * mm});
            skLineSegment(sketch, "E394", {"start": v(-15.81, -142.53) * mm, "end": v(-15.88, -143.2) * mm});
            skLineSegment(sketch, "E395", {"start": v(-15.88, -143.2) * mm, "end": v(-15.88, -143.26) * mm});
            skLineSegment(sketch, "E396", {"start": v(-15.88, -143.26) * mm, "end": v(-15.45, -143.26) * mm});
            skLineSegment(sketch, "E397", {"start": v(-15.45, -143.26) * mm, "end": v(-15.4, -142.8) * mm});
            skLineSegment(sketch, "E398", {"start": v(-15.4, -142.8) * mm, "end": v(-15.28, -142.46) * mm});
            skLineSegment(sketch, "E399", {"start": v(-15.28, -142.46) * mm, "end": v(-15.08, -142.26) * mm});
            skLineSegment(sketch, "E400", {"start": v(-15.08, -142.26) * mm, "end": v(-14.79, -142.19) * mm});
            skLineSegment(sketch, "E401", {"start": v(-14.79, -142.19) * mm, "end": v(-14.53, -142.25) * mm});
            skLineSegment(sketch, "E402", {"start": v(-14.53, -142.25) * mm, "end": v(-14.35, -142.4) * mm});
            skLineSegment(sketch, "E403", {"start": v(-14.35, -142.4) * mm, "end": v(-14.23, -142.64) * mm});
            skLineSegment(sketch, "E404", {"start": v(-14.23, -142.64) * mm, "end": v(-14.19, -142.97) * mm});
            skLineSegment(sketch, "E405", {"start": v(-14.19, -142.97) * mm, "end": v(-14.23, -143.33) * mm});
            skLineSegment(sketch, "E406", {"start": v(-14.23, -143.33) * mm, "end": v(-14.35, -143.56) * mm});
            skLineSegment(sketch, "E407", {"start": v(-14.35, -143.56) * mm, "end": v(-14.56, -143.7) * mm});
            skLineSegment(sketch, "E408", {"start": v(-14.56, -143.7) * mm, "end": v(-14.84, -143.75) * mm});
            skLineSegment(sketch, "E409", {"start": v(-14.84, -143.75) * mm, "end": v(-15.03, -143.74) * mm});
            skLineSegment(sketch, "E410", {"start": v(-15.03, -143.74) * mm, "end": v(-15.03, -144.31) * mm});
            skLineSegment(sketch, "E411", {"start": v(-15.03, -144.31) * mm, "end": v(-14.79, -144.3) * mm});
            skLineSegment(sketch, "E412", {"start": v(-14.79, -144.3) * mm, "end": v(-14.48, -144.36) * mm});
            skLineSegment(sketch, "E413", {"start": v(-14.48, -144.36) * mm, "end": v(-14.25, -144.54) * mm});
            skLineSegment(sketch, "E414", {"start": v(-14.25, -144.54) * mm, "end": v(-14.11, -144.82) * mm});
            skLineSegment(sketch, "E415", {"start": v(-14.11, -144.82) * mm, "end": v(-14.06, -145.19) * mm});
            skLineSegment(sketch, "E416", {"start": v(-14.06, -145.19) * mm, "end": v(-14.12, -145.6) * mm});
            skLineSegment(sketch, "E417", {"start": v(-14.12, -145.6) * mm, "end": v(-14.26, -145.91) * mm});
            skLineSegment(sketch, "E418", {"start": v(-14.26, -145.91) * mm, "end": v(-14.48, -146.1) * mm});
            skLineSegment(sketch, "E419", {"start": v(-14.48, -146.1) * mm, "end": v(-14.78, -146.17) * mm});
            skLineSegment(sketch, "E420", {"start": v(-14.78, -146.17) * mm, "end": v(-15.1, -146.1) * mm});
            skLineSegment(sketch, "E421", {"start": v(-15.1, -146.1) * mm, "end": v(-15.32, -145.88) * mm});
            skLineSegment(sketch, "E422", {"start": v(-15.32, -145.88) * mm, "end": v(-15.46, -145.54) * mm});
            skLineSegment(sketch, "E423", {"start": v(-15.46, -145.54) * mm, "end": v(-15.51, -145.06) * mm});
            skLineSegment(sketch, "E424", {"start": v(-15.51, -145.06) * mm, "end": v(-15.96, -145.06) * mm});
            skLineSegment(sketch, "E425", {"start": v(-12.46, -146.63) * mm, "end": v(-12.07, -146.63) * mm});
            skLineSegment(sketch, "E426", {"start": v(-12.07, -146.63) * mm, "end": v(-12.07, -144.05) * mm});
            skLineSegment(sketch, "E427", {"start": v(-12.07, -144.05) * mm, "end": v(-12.04, -143.66) * mm});
            skLineSegment(sketch, "E428", {"start": v(-12.04, -143.66) * mm, "end": v(-11.97, -143.38) * mm});
            skLineSegment(sketch, "E429", {"start": v(-11.97, -143.38) * mm, "end": v(-11.86, -143.21) * mm});
            skLineSegment(sketch, "E430", {"start": v(-11.86, -143.21) * mm, "end": v(-11.71, -143.15) * mm});
            skLineSegment(sketch, "E431", {"start": v(-11.71, -143.15) * mm, "end": v(-11.6, -143.2) * mm});
            skLineSegment(sketch, "E432", {"start": v(-11.6, -143.2) * mm, "end": v(-11.51, -143.35) * mm});
            skLineSegment(sketch, "E433", {"start": v(-11.51, -143.35) * mm, "end": v(-11.47, -143.6) * mm});
            skLineSegment(sketch, "E434", {"start": v(-11.47, -143.6) * mm, "end": v(-11.46, -143.92) * mm});
            skLineSegment(sketch, "E435", {"start": v(-11.46, -143.92) * mm, "end": v(-11.46, -146.63) * mm});
            skLineSegment(sketch, "E436", {"start": v(-11.46, -146.63) * mm, "end": v(-11.09, -146.63) * mm});
            skLineSegment(sketch, "E437", {"start": v(-11.09, -146.63) * mm, "end": v(-11.09, -144.05) * mm});
            skLineSegment(sketch, "E438", {"start": v(-11.09, -144.05) * mm, "end": v(-11.06, -143.67) * mm});
            skLineSegment(sketch, "E439", {"start": v(-11.06, -143.67) * mm, "end": v(-10.99, -143.38) * mm});
            skLineSegment(sketch, "E440", {"start": v(-10.99, -143.38) * mm, "end": v(-10.87, -143.21) * mm});
            skLineSegment(sketch, "E441", {"start": v(-10.87, -143.21) * mm, "end": v(-10.73, -143.15) * mm});
            skLineSegment(sketch, "E442", {"start": v(-10.73, -143.15) * mm, "end": v(-10.6, -143.2) * mm});
            skLineSegment(sketch, "E443", {"start": v(-10.6, -143.2) * mm, "end": v(-10.53, -143.35) * mm});
            skLineSegment(sketch, "E444", {"start": v(-10.53, -143.35) * mm, "end": v(-10.48, -143.92) * mm});
            skLineSegment(sketch, "E445", {"start": v(-10.48, -143.92) * mm, "end": v(-10.48, -146.63) * mm});
            skLineSegment(sketch, "E446", {"start": v(-10.48, -146.63) * mm, "end": v(-10.08, -146.63) * mm});
            skLineSegment(sketch, "E447", {"start": v(-10.08, -146.63) * mm, "end": v(-10.08, -143.96) * mm});
            skLineSegment(sketch, "E448", {"start": v(-10.08, -143.96) * mm, "end": v(-10.1, -143.4) * mm});
            skLineSegment(sketch, "E449", {"start": v(-10.1, -143.4) * mm, "end": v(-10.19, -142.98) * mm});
            skLineSegment(sketch, "E450", {"start": v(-10.19, -142.98) * mm, "end": v(-10.34, -142.72) * mm});
            skLineSegment(sketch, "E451", {"start": v(-10.34, -142.72) * mm, "end": v(-10.6, -142.63) * mm});
            skLineSegment(sketch, "E452", {"start": v(-10.6, -142.63) * mm, "end": v(-10.9, -142.77) * mm});
            skLineSegment(sketch, "E453", {"start": v(-10.9, -142.77) * mm, "end": v(-11.13, -143.2) * mm});
            skLineSegment(sketch, "E454", {"start": v(-11.13, -143.2) * mm, "end": v(-11.3, -142.78) * mm});
            skLineSegment(sketch, "E455", {"start": v(-11.3, -142.78) * mm, "end": v(-11.61, -142.63) * mm});
            skLineSegment(sketch, "E456", {"start": v(-11.61, -142.63) * mm, "end": v(-11.9, -142.77) * mm});
            skLineSegment(sketch, "E457", {"start": v(-11.9, -142.77) * mm, "end": v(-12.08, -143.18) * mm});
            skLineSegment(sketch, "E458", {"start": v(-12.08, -143.18) * mm, "end": v(-12.08, -142.77) * mm});
            skLineSegment(sketch, "E459", {"start": v(-12.08, -142.77) * mm, "end": v(-12.46, -142.77) * mm});
            skLineSegment(sketch, "E460", {"start": v(-12.46, -142.77) * mm, "end": v(-12.46, -146.63) * mm});
            skLineSegment(sketch, "E461", {"start": v(-9.02, -146.63) * mm, "end": v(-8.62, -146.63) * mm});
            skLineSegment(sketch, "E462", {"start": v(-8.62, -146.63) * mm, "end": v(-8.62, -144.05) * mm});
            skLineSegment(sketch, "E463", {"start": v(-8.62, -144.05) * mm, "end": v(-8.6, -143.66) * mm});
            skLineSegment(sketch, "E464", {"start": v(-8.6, -143.66) * mm, "end": v(-8.52, -143.38) * mm});
            skLineSegment(sketch, "E465", {"start": v(-8.52, -143.38) * mm, "end": v(-8.4, -143.21) * mm});
            skLineSegment(sketch, "E466", {"start": v(-8.4, -143.21) * mm, "end": v(-8.26, -143.15) * mm});
            skLineSegment(sketch, "E467", {"start": v(-8.26, -143.15) * mm, "end": v(-8.14, -143.2) * mm});
            skLineSegment(sketch, "E468", {"start": v(-8.14, -143.2) * mm, "end": v(-8.06, -143.35) * mm});
            skLineSegment(sketch, "E469", {"start": v(-8.06, -143.35) * mm, "end": v(-8.03, -143.6) * mm});
            skLineSegment(sketch, "E470", {"start": v(-8.03, -143.6) * mm, "end": v(-8.01, -143.92) * mm});
            skLineSegment(sketch, "E471", {"start": v(-8.01, -143.92) * mm, "end": v(-8.01, -146.63) * mm});
            skLineSegment(sketch, "E472", {"start": v(-8.01, -146.63) * mm, "end": v(-7.64, -146.63) * mm});
            skLineSegment(sketch, "E473", {"start": v(-7.64, -146.63) * mm, "end": v(-7.64, -144.05) * mm});
            skLineSegment(sketch, "E474", {"start": v(-7.64, -144.05) * mm, "end": v(-7.61, -143.67) * mm});
            skLineSegment(sketch, "E475", {"start": v(-7.61, -143.67) * mm, "end": v(-7.54, -143.38) * mm});
            skLineSegment(sketch, "E476", {"start": v(-7.54, -143.38) * mm, "end": v(-7.42, -143.21) * mm});
            skLineSegment(sketch, "E477", {"start": v(-7.42, -143.21) * mm, "end": v(-7.28, -143.15) * mm});
            skLineSegment(sketch, "E478", {"start": v(-7.28, -143.15) * mm, "end": v(-7.16, -143.2) * mm});
            skLineSegment(sketch, "E479", {"start": v(-7.16, -143.2) * mm, "end": v(-7.08, -143.35) * mm});
            skLineSegment(sketch, "E480", {"start": v(-7.08, -143.35) * mm, "end": v(-7.03, -143.92) * mm});
            skLineSegment(sketch, "E481", {"start": v(-7.03, -143.92) * mm, "end": v(-7.03, -146.63) * mm});
            skLineSegment(sketch, "E482", {"start": v(-7.03, -146.63) * mm, "end": v(-6.63, -146.63) * mm});
            skLineSegment(sketch, "E483", {"start": v(-6.63, -146.63) * mm, "end": v(-6.63, -143.96) * mm});
            skLineSegment(sketch, "E484", {"start": v(-6.63, -143.96) * mm, "end": v(-6.66, -143.4) * mm});
            skLineSegment(sketch, "E485", {"start": v(-6.66, -143.4) * mm, "end": v(-6.74, -142.98) * mm});
            skLineSegment(sketch, "E486", {"start": v(-6.74, -142.98) * mm, "end": v(-6.9, -142.72) * mm});
            skLineSegment(sketch, "E487", {"start": v(-6.9, -142.72) * mm, "end": v(-7.15, -142.63) * mm});
            skLineSegment(sketch, "E488", {"start": v(-7.15, -142.63) * mm, "end": v(-7.45, -142.77) * mm});
            skLineSegment(sketch, "E489", {"start": v(-7.45, -142.77) * mm, "end": v(-7.68, -143.2) * mm});
            skLineSegment(sketch, "E490", {"start": v(-7.68, -143.2) * mm, "end": v(-7.86, -142.78) * mm});
            skLineSegment(sketch, "E491", {"start": v(-7.86, -142.78) * mm, "end": v(-8.16, -142.63) * mm});
            skLineSegment(sketch, "E492", {"start": v(-8.16, -142.63) * mm, "end": v(-8.44, -142.77) * mm});
            skLineSegment(sketch, "E493", {"start": v(-8.44, -142.77) * mm, "end": v(-8.63, -143.18) * mm});
            skLineSegment(sketch, "E494", {"start": v(-8.63, -143.18) * mm, "end": v(-8.63, -142.77) * mm});
            skLineSegment(sketch, "E495", {"start": v(-8.63, -142.77) * mm, "end": v(-9.02, -142.77) * mm});
            skLineSegment(sketch, "E496", {"start": v(-9.02, -142.77) * mm, "end": v(-9.02, -146.63) * mm});
            skLineSegment(sketch, "E497", {"start": v(-29.75, -155.27) * mm, "end": v(-29.37, -155.27) * mm});
            skLineSegment(sketch, "E498", {"start": v(-29.37, -155.27) * mm, "end": v(-29.37, -150.73) * mm});
            skLineSegment(sketch, "E499", {"start": v(-29.37, -150.73) * mm, "end": v(-28.74, -155.27) * mm});
            skLineSegment(sketch, "E500", {"start": v(-28.74, -155.27) * mm, "end": v(-28.31, -155.27) * mm});
            skLineSegment(sketch, "E501", {"start": v(-28.31, -155.27) * mm, "end": v(-27.68, -150.73) * mm});
            skLineSegment(sketch, "E502", {"start": v(-27.68, -150.73) * mm, "end": v(-27.68, -155.27) * mm});
            skLineSegment(sketch, "E503", {"start": v(-27.68, -155.27) * mm, "end": v(-27.3, -155.27) * mm});
            skLineSegment(sketch, "E504", {"start": v(-27.3, -155.27) * mm, "end": v(-27.3, -150.27) * mm});
            skLineSegment(sketch, "E505", {"start": v(-27.3, -150.27) * mm, "end": v(-27.9, -150.27) * mm});
            skLineSegment(sketch, "E506", {"start": v(-27.9, -150.27) * mm, "end": v(-28.53, -154.68) * mm});
            skLineSegment(sketch, "E507", {"start": v(-28.53, -154.68) * mm, "end": v(-29.15, -150.27) * mm});
            skLineSegment(sketch, "E508", {"start": v(-29.15, -150.27) * mm, "end": v(-29.75, -150.27) * mm});
            skLineSegment(sketch, "E509", {"start": v(-29.75, -150.27) * mm, "end": v(-29.75, -155.27) * mm});
            skLineSegment(sketch, "E510", {"start": v(-24.53, -154.77) * mm, "end": v(-24.53, -154.79) * mm});
            skLineSegment(sketch, "E511", {"start": v(-24.53, -154.79) * mm, "end": v(-24.5, -155.03) * mm});
            skLineSegment(sketch, "E512", {"start": v(-24.5, -155.03) * mm, "end": v(-24.43, -155.2) * mm});
            skLineSegment(sketch, "E513", {"start": v(-24.43, -155.2) * mm, "end": v(-24.12, -155.34) * mm});
            skLineSegment(sketch, "E514", {"start": v(-24.12, -155.34) * mm, "end": v(-23.88, -155.29) * mm});
            skLineSegment(sketch, "E515", {"start": v(-23.88, -155.29) * mm, "end": v(-23.88, -154.8) * mm});
            skLineSegment(sketch, "E516", {"start": v(-23.88, -154.8) * mm, "end": v(-23.98, -154.82) * mm});
            skLineSegment(sketch, "E517", {"start": v(-23.98, -154.82) * mm, "end": v(-24.12, -154.72) * mm});
            skLineSegment(sketch, "E518", {"start": v(-24.12, -154.72) * mm, "end": v(-24.15, -154.44) * mm});
            skLineSegment(sketch, "E519", {"start": v(-24.15, -154.44) * mm, "end": v(-24.15, -152.43) * mm});
            skLineSegment(sketch, "E520", {"start": v(-24.15, -152.43) * mm, "end": v(-24.2, -151.92) * mm});
            skLineSegment(sketch, "E521", {"start": v(-24.2, -151.92) * mm, "end": v(-24.38, -151.56) * mm});
            skLineSegment(sketch, "E522", {"start": v(-24.38, -151.56) * mm, "end": v(-24.67, -151.35) * mm});
            skLineSegment(sketch, "E523", {"start": v(-24.67, -151.35) * mm, "end": v(-25.1, -151.27) * mm});
            skLineSegment(sketch, "E524", {"start": v(-25.1, -151.27) * mm, "end": v(-25.5, -151.35) * mm});
            skLineSegment(sketch, "E525", {"start": v(-25.5, -151.35) * mm, "end": v(-25.81, -151.6) * mm});
            skLineSegment(sketch, "E526", {"start": v(-25.81, -151.6) * mm, "end": v(-26, -151.98) * mm});
            skLineSegment(sketch, "E527", {"start": v(-26, -151.98) * mm, "end": v(-26.07, -152.48) * mm});
            skLineSegment(sketch, "E528", {"start": v(-26.07, -152.48) * mm, "end": v(-26.07, -152.53) * mm});
            skLineSegment(sketch, "E529", {"start": v(-26.07, -152.53) * mm, "end": v(-25.68, -152.53) * mm});
            skLineSegment(sketch, "E530", {"start": v(-25.68, -152.53) * mm, "end": v(-25.64, -152.22) * mm});
            skLineSegment(sketch, "E531", {"start": v(-25.64, -152.22) * mm, "end": v(-25.54, -152) * mm});
            skLineSegment(sketch, "E532", {"start": v(-25.54, -152) * mm, "end": v(-25.36, -151.88) * mm});
            skLineSegment(sketch, "E533", {"start": v(-25.36, -151.88) * mm, "end": v(-25.11, -151.83) * mm});
            skLineSegment(sketch, "E534", {"start": v(-25.11, -151.83) * mm, "end": v(-24.87, -151.86) * mm});
            skLineSegment(sketch, "E535", {"start": v(-24.87, -151.86) * mm, "end": v(-24.7, -151.97) * mm});
            skLineSegment(sketch, "E536", {"start": v(-24.7, -151.97) * mm, "end": v(-24.6, -152.16) * mm});
            skLineSegment(sketch, "E537", {"start": v(-24.6, -152.16) * mm, "end": v(-24.56, -152.42) * mm});
            skLineSegment(sketch, "E538", {"start": v(-24.56, -152.42) * mm, "end": v(-24.58, -152.72) * mm});
            skLineSegment(sketch, "E539", {"start": v(-24.58, -152.72) * mm, "end": v(-24.66, -152.87) * mm});
            skLineSegment(sketch, "E540", {"start": v(-24.66, -152.87) * mm, "end": v(-24.86, -152.95) * mm});
            skLineSegment(sketch, "E541", {"start": v(-24.86, -152.95) * mm, "end": v(-25.22, -153) * mm});
            skLineSegment(sketch, "E542", {"start": v(-25.22, -153) * mm, "end": v(-25.64, -153.13) * mm});
            skLineSegment(sketch, "E543", {"start": v(-25.64, -153.13) * mm, "end": v(-25.94, -153.36) * mm});
            skLineSegment(sketch, "E544", {"start": v(-25.94, -153.36) * mm, "end": v(-26.12, -153.72) * mm});
            skLineSegment(sketch, "E545", {"start": v(-26.12, -153.72) * mm, "end": v(-26.17, -154.26) * mm});
            skLineSegment(sketch, "E546", {"start": v(-26.17, -154.26) * mm, "end": v(-26.12, -154.73) * mm});
            skLineSegment(sketch, "E547", {"start": v(-26.12, -154.73) * mm, "end": v(-25.97, -155.09) * mm});
            skLineSegment(sketch, "E548", {"start": v(-25.97, -155.09) * mm, "end": v(-25.73, -155.3) * mm});
            skLineSegment(sketch, "E549", {"start": v(-25.73, -155.3) * mm, "end": v(-25.39, -155.39) * mm});
            skLineSegment(sketch, "E550", {"start": v(-25.39, -155.39) * mm, "end": v(-24.93, -155.24) * mm});
            skLineSegment(sketch, "E551", {"start": v(-24.93, -155.24) * mm, "end": v(-24.53, -154.77) * mm});
            skLineSegment(sketch, "E552", {"start": v(-24.58, -153.92) * mm, "end": v(-24.64, -154.3) * mm});
            skLineSegment(sketch, "E553", {"start": v(-24.64, -154.3) * mm, "end": v(-24.8, -154.58) * mm});
            skLineSegment(sketch, "E554", {"start": v(-24.8, -154.58) * mm, "end": v(-25.03, -154.77) * mm});
            skLineSegment(sketch, "E555", {"start": v(-25.03, -154.77) * mm, "end": v(-25.32, -154.83) * mm});
            skLineSegment(sketch, "E556", {"start": v(-25.32, -154.83) * mm, "end": v(-25.5, -154.8) * mm});
            skLineSegment(sketch, "E557", {"start": v(-25.5, -154.8) * mm, "end": v(-25.63, -154.68) * mm});
            skLineSegment(sketch, "E558", {"start": v(-25.63, -154.68) * mm, "end": v(-25.72, -154.48) * mm});
            skLineSegment(sketch, "E559", {"start": v(-25.72, -154.48) * mm, "end": v(-25.74, -154.2) * mm});
            skLineSegment(sketch, "E560", {"start": v(-25.74, -154.2) * mm, "end": v(-25.72, -153.95) * mm});
            skLineSegment(sketch, "E561", {"start": v(-25.72, -153.95) * mm, "end": v(-25.64, -153.77) * mm});
            skLineSegment(sketch, "E562", {"start": v(-25.64, -153.77) * mm, "end": v(-25.33, -153.56) * mm});
            skLineSegment(sketch, "E563", {"start": v(-25.33, -153.56) * mm, "end": v(-24.93, -153.48) * mm});
            skLineSegment(sketch, "E564", {"start": v(-24.93, -153.48) * mm, "end": v(-24.58, -153.3) * mm});
            skLineSegment(sketch, "E565", {"start": v(-24.58, -153.3) * mm, "end": v(-24.58, -153.92) * mm});
            skLineSegment(sketch, "E566", {"start": v(-22.06, -152.07) * mm, "end": v(-22.06, -154.01) * mm});
            skLineSegment(sketch, "E567", {"start": v(-22.06, -154.01) * mm, "end": v(-22.03, -154.64) * mm});
            skLineSegment(sketch, "E568", {"start": v(-22.03, -154.64) * mm, "end": v(-21.9, -155.07) * mm});
            skLineSegment(sketch, "E569", {"start": v(-21.9, -155.07) * mm, "end": v(-21.62, -155.32) * mm});
            skLineSegment(sketch, "E570", {"start": v(-21.62, -155.32) * mm, "end": v(-21.16, -155.4) * mm});
            skLineSegment(sketch, "E571", {"start": v(-21.16, -155.4) * mm, "end": v(-20.65, -155.37) * mm});
            skLineSegment(sketch, "E572", {"start": v(-20.65, -155.37) * mm, "end": v(-20.65, -154.83) * mm});
            skLineSegment(sketch, "E573", {"start": v(-20.65, -154.83) * mm, "end": v(-21.02, -154.87) * mm});
            skLineSegment(sketch, "E574", {"start": v(-21.02, -154.87) * mm, "end": v(-21.36, -154.81) * mm});
            skLineSegment(sketch, "E575", {"start": v(-21.36, -154.81) * mm, "end": v(-21.54, -154.63) * mm});
            skLineSegment(sketch, "E576", {"start": v(-21.54, -154.63) * mm, "end": v(-21.62, -154.33) * mm});
            skLineSegment(sketch, "E577", {"start": v(-21.62, -154.33) * mm, "end": v(-21.63, -153.9) * mm});
            skLineSegment(sketch, "E578", {"start": v(-21.63, -153.9) * mm, "end": v(-21.63, -152.07) * mm});
            skLineSegment(sketch, "E579", {"start": v(-21.63, -152.07) * mm, "end": v(-20.65, -152.07) * mm});
            skLineSegment(sketch, "E580", {"start": v(-20.65, -152.07) * mm, "end": v(-20.65, -151.53) * mm});
            skLineSegment(sketch, "E581", {"start": v(-20.65, -151.53) * mm, "end": v(-21.63, -151.53) * mm});
            skLineSegment(sketch, "E582", {"start": v(-21.63, -151.53) * mm, "end": v(-21.63, -150.4) * mm});
            skLineSegment(sketch, "E583", {"start": v(-21.63, -150.4) * mm, "end": v(-22.06, -150.4) * mm});
            skLineSegment(sketch, "E584", {"start": v(-22.06, -150.4) * mm, "end": v(-22.06, -151.53) * mm});
            skLineSegment(sketch, "E585", {"start": v(-22.06, -151.53) * mm, "end": v(-22.8, -151.53) * mm});
            skLineSegment(sketch, "E586", {"start": v(-22.8, -151.53) * mm, "end": v(-22.8, -152.07) * mm});
            skLineSegment(sketch, "E587", {"start": v(-22.8, -152.07) * mm, "end": v(-22.06, -152.07) * mm});
            skLineSegment(sketch, "E588", {"start": v(-18.81, -153.52) * mm, "end": v(-17.09, -153.52) * mm});
            skLineSegment(sketch, "E589", {"start": v(-17.09, -153.52) * mm, "end": v(-17.09, -153.23) * mm});
            skLineSegment(sketch, "E590", {"start": v(-17.09, -153.23) * mm, "end": v(-17.16, -152.4) * mm});
            skLineSegment(sketch, "E591", {"start": v(-17.16, -152.4) * mm, "end": v(-17.38, -151.78) * mm});
            skLineSegment(sketch, "E592", {"start": v(-17.38, -151.78) * mm, "end": v(-17.72, -151.4) * mm});
            skLineSegment(sketch, "E593", {"start": v(-17.72, -151.4) * mm, "end": v(-18.18, -151.27) * mm});
            skLineSegment(sketch, "E594", {"start": v(-18.18, -151.27) * mm, "end": v(-18.62, -151.41) * mm});
            skLineSegment(sketch, "E595", {"start": v(-18.62, -151.41) * mm, "end": v(-18.97, -151.81) * mm});
            skLineSegment(sketch, "E596", {"start": v(-18.97, -151.81) * mm, "end": v(-19.19, -152.47) * mm});
            skLineSegment(sketch, "E597", {"start": v(-19.19, -152.47) * mm, "end": v(-19.27, -153.33) * mm});
            skLineSegment(sketch, "E598", {"start": v(-19.27, -153.33) * mm, "end": v(-19.2, -154.22) * mm});
            skLineSegment(sketch, "E599", {"start": v(-19.2, -154.22) * mm, "end": v(-18.97, -154.87) * mm});
            skLineSegment(sketch, "E600", {"start": v(-18.97, -154.87) * mm, "end": v(-18.63, -155.27) * mm});
            skLineSegment(sketch, "E601", {"start": v(-18.63, -155.27) * mm, "end": v(-18.2, -155.4) * mm});
            skLineSegment(sketch, "E602", {"start": v(-18.2, -155.4) * mm, "end": v(-17.81, -155.32) * mm});
            skLineSegment(sketch, "E603", {"start": v(-17.81, -155.32) * mm, "end": v(-17.5, -155.07) * mm});
            skLineSegment(sketch, "E604", {"start": v(-17.5, -155.07) * mm, "end": v(-17.27, -154.68) * mm});
            skLineSegment(sketch, "E605", {"start": v(-17.27, -154.68) * mm, "end": v(-17.13, -154.16) * mm});
            skLineSegment(sketch, "E606", {"start": v(-17.13, -154.16) * mm, "end": v(-17.56, -154.16) * mm});
            skLineSegment(sketch, "E607", {"start": v(-17.56, -154.16) * mm, "end": v(-17.65, -154.45) * mm});
            skLineSegment(sketch, "E608", {"start": v(-17.65, -154.45) * mm, "end": v(-17.78, -154.67) * mm});
            skLineSegment(sketch, "E609", {"start": v(-17.78, -154.67) * mm, "end": v(-18.14, -154.84) * mm});
            skLineSegment(sketch, "E610", {"start": v(-18.14, -154.84) * mm, "end": v(-18.42, -154.76) * mm});
            skLineSegment(sketch, "E611", {"start": v(-18.42, -154.76) * mm, "end": v(-18.63, -154.5) * mm});
            skLineSegment(sketch, "E612", {"start": v(-18.63, -154.5) * mm, "end": v(-18.77, -154.1) * mm});
            skLineSegment(sketch, "E613", {"start": v(-18.77, -154.1) * mm, "end": v(-18.81, -153.54) * mm});
            skLineSegment(sketch, "E614", {"start": v(-18.81, -153.54) * mm, "end": v(-18.81, -153.52) * mm});
            skLineSegment(sketch, "E615", {"start": v(-18.81, -152.99) * mm, "end": v(-18.76, -152.5) * mm});
            skLineSegment(sketch, "E616", {"start": v(-18.76, -152.5) * mm, "end": v(-18.63, -152.12) * mm});
            skLineSegment(sketch, "E617", {"start": v(-18.63, -152.12) * mm, "end": v(-18.43, -151.9) * mm});
            skLineSegment(sketch, "E618", {"start": v(-18.43, -151.9) * mm, "end": v(-18.16, -151.82) * mm});
            skLineSegment(sketch, "E619", {"start": v(-18.16, -151.82) * mm, "end": v(-17.9, -151.9) * mm});
            skLineSegment(sketch, "E620", {"start": v(-17.9, -151.9) * mm, "end": v(-17.7, -152.12) * mm});
            skLineSegment(sketch, "E621", {"start": v(-17.7, -152.12) * mm, "end": v(-17.58, -152.5) * mm});
            skLineSegment(sketch, "E622", {"start": v(-17.58, -152.5) * mm, "end": v(-17.54, -152.99) * mm});
            skLineSegment(sketch, "E623", {"start": v(-17.54, -152.99) * mm, "end": v(-18.81, -152.99) * mm});
            skLineSegment(sketch, "E624", {"start": v(-15.58, -155.27) * mm, "end": v(-15.15, -155.27) * mm});
            skLineSegment(sketch, "E625", {"start": v(-15.15, -155.27) * mm, "end": v(-15.15, -153.06) * mm});
            skLineSegment(sketch, "E626", {"start": v(-15.15, -153.06) * mm, "end": v(-15.1, -152.53) * mm});
            skLineSegment(sketch, "E627", {"start": v(-15.1, -152.53) * mm, "end": v(-14.97, -152.15) * mm});
            skLineSegment(sketch, "E628", {"start": v(-14.97, -152.15) * mm, "end": v(-14.76, -151.91) * mm});
            skLineSegment(sketch, "E629", {"start": v(-14.76, -151.91) * mm, "end": v(-14.47, -151.84) * mm});
            skLineSegment(sketch, "E630", {"start": v(-14.47, -151.84) * mm, "end": v(-14.25, -151.89) * mm});
            skLineSegment(sketch, "E631", {"start": v(-14.25, -151.89) * mm, "end": v(-14.1, -152.03) * mm});
            skLineSegment(sketch, "E632", {"start": v(-14.1, -152.03) * mm, "end": v(-14, -152.28) * mm});
            skLineSegment(sketch, "E633", {"start": v(-14, -152.28) * mm, "end": v(-13.96, -152.6) * mm});
            skLineSegment(sketch, "E634", {"start": v(-13.96, -152.6) * mm, "end": v(-13.52, -152.6) * mm});
            skLineSegment(sketch, "E635", {"start": v(-13.52, -152.6) * mm, "end": v(-13.58, -152.02) * mm});
            skLineSegment(sketch, "E636", {"start": v(-13.58, -152.02) * mm, "end": v(-13.74, -151.6) * mm});
            skLineSegment(sketch, "E637", {"start": v(-13.74, -151.6) * mm, "end": v(-14.01, -151.35) * mm});
            skLineSegment(sketch, "E638", {"start": v(-14.01, -151.35) * mm, "end": v(-14.38, -151.27) * mm});
            skLineSegment(sketch, "E639", {"start": v(-14.38, -151.27) * mm, "end": v(-14.63, -151.32) * mm});
            skLineSegment(sketch, "E640", {"start": v(-14.63, -151.32) * mm, "end": v(-14.85, -151.47) * mm});
            skLineSegment(sketch, "E641", {"start": v(-14.85, -151.47) * mm, "end": v(-15.04, -151.71) * mm});
            skLineSegment(sketch, "E642", {"start": v(-15.04, -151.71) * mm, "end": v(-15.19, -152.04) * mm});
            skLineSegment(sketch, "E643", {"start": v(-15.19, -152.04) * mm, "end": v(-15.19, -151.4) * mm});
            skLineSegment(sketch, "E644", {"start": v(-15.19, -151.4) * mm, "end": v(-15.58, -151.4) * mm});
            skLineSegment(sketch, "E645", {"start": v(-15.58, -151.4) * mm, "end": v(-15.58, -155.27) * mm});
            skLineSegment(sketch, "E646", {"start": v(-10.98, -154.74) * mm, "end": v(-10.98, -151.53) * mm});
            skLineSegment(sketch, "E647", {"start": v(-10.98, -151.53) * mm, "end": v(-12.08, -151.53) * mm});
            skLineSegment(sketch, "E648", {"start": v(-12.08, -151.53) * mm, "end": v(-12.08, -152.07) * mm});
            skLineSegment(sketch, "E649", {"start": v(-12.08, -152.07) * mm, "end": v(-11.4, -152.07) * mm});
            skLineSegment(sketch, "E650", {"start": v(-11.4, -152.07) * mm, "end": v(-11.4, -154.74) * mm});
            skLineSegment(sketch, "E651", {"start": v(-11.4, -154.74) * mm, "end": v(-12.29, -154.74) * mm});
            skLineSegment(sketch, "E652", {"start": v(-12.29, -154.74) * mm, "end": v(-12.29, -155.27) * mm});
            skLineSegment(sketch, "E653", {"start": v(-12.29, -155.27) * mm, "end": v(-10.08, -155.27) * mm});
            skLineSegment(sketch, "E654", {"start": v(-10.08, -155.27) * mm, "end": v(-10.08, -154.74) * mm});
            skLineSegment(sketch, "E655", {"start": v(-10.08, -154.74) * mm, "end": v(-10.98, -154.74) * mm});
            skLineSegment(sketch, "E656", {"start": v(-10.96, -150.1) * mm, "end": v(-11.42, -150.1) * mm});
            skLineSegment(sketch, "E657", {"start": v(-11.42, -150.1) * mm, "end": v(-11.42, -150.82) * mm});
            skLineSegment(sketch, "E658", {"start": v(-11.42, -150.82) * mm, "end": v(-10.96, -150.82) * mm});
            skLineSegment(sketch, "E659", {"start": v(-10.96, -150.82) * mm, "end": v(-10.96, -150.1) * mm});
            skLineSegment(sketch, "E660", {"start": v(-7.28, -154.77) * mm, "end": v(-7.28, -154.79) * mm});
            skLineSegment(sketch, "E661", {"start": v(-7.28, -154.79) * mm, "end": v(-7.26, -155.03) * mm});
            skLineSegment(sketch, "E662", {"start": v(-7.26, -155.03) * mm, "end": v(-7.18, -155.2) * mm});
            skLineSegment(sketch, "E663", {"start": v(-7.18, -155.2) * mm, "end": v(-6.87, -155.34) * mm});
            skLineSegment(sketch, "E664", {"start": v(-6.87, -155.34) * mm, "end": v(-6.63, -155.29) * mm});
            skLineSegment(sketch, "E665", {"start": v(-6.63, -155.29) * mm, "end": v(-6.63, -154.8) * mm});
            skLineSegment(sketch, "E666", {"start": v(-6.63, -154.8) * mm, "end": v(-6.74, -154.82) * mm});
            skLineSegment(sketch, "E667", {"start": v(-6.74, -154.82) * mm, "end": v(-6.87, -154.72) * mm});
            skLineSegment(sketch, "E668", {"start": v(-6.87, -154.72) * mm, "end": v(-6.9, -154.44) * mm});
            skLineSegment(sketch, "E669", {"start": v(-6.9, -154.44) * mm, "end": v(-6.9, -152.43) * mm});
            skLineSegment(sketch, "E670", {"start": v(-6.9, -152.43) * mm, "end": v(-6.96, -151.92) * mm});
            skLineSegment(sketch, "E671", {"start": v(-6.96, -151.92) * mm, "end": v(-7.13, -151.56) * mm});
            skLineSegment(sketch, "E672", {"start": v(-7.13, -151.56) * mm, "end": v(-7.43, -151.35) * mm});
            skLineSegment(sketch, "E673", {"start": v(-7.43, -151.35) * mm, "end": v(-7.85, -151.27) * mm});
            skLineSegment(sketch, "E674", {"start": v(-7.85, -151.27) * mm, "end": v(-8.26, -151.35) * mm});
            skLineSegment(sketch, "E675", {"start": v(-8.26, -151.35) * mm, "end": v(-8.56, -151.6) * mm});
            skLineSegment(sketch, "E676", {"start": v(-8.56, -151.6) * mm, "end": v(-8.76, -151.98) * mm});
            skLineSegment(sketch, "E677", {"start": v(-8.76, -151.98) * mm, "end": v(-8.82, -152.48) * mm});
            skLineSegment(sketch, "E678", {"start": v(-8.82, -152.48) * mm, "end": v(-8.82, -152.53) * mm});
            skLineSegment(sketch, "E679", {"start": v(-8.82, -152.53) * mm, "end": v(-8.43, -152.53) * mm});
            skLineSegment(sketch, "E680", {"start": v(-8.43, -152.53) * mm, "end": v(-8.4, -152.22) * mm});
            skLineSegment(sketch, "E681", {"start": v(-8.4, -152.22) * mm, "end": v(-8.3, -152) * mm});
            skLineSegment(sketch, "E682", {"start": v(-8.3, -152) * mm, "end": v(-8.11, -151.88) * mm});
            skLineSegment(sketch, "E683", {"start": v(-8.11, -151.88) * mm, "end": v(-7.86, -151.83) * mm});
            skLineSegment(sketch, "E684", {"start": v(-7.86, -151.83) * mm, "end": v(-7.62, -151.86) * mm});
            skLineSegment(sketch, "E685", {"start": v(-7.62, -151.86) * mm, "end": v(-7.45, -151.97) * mm});
            skLineSegment(sketch, "E686", {"start": v(-7.45, -151.97) * mm, "end": v(-7.35, -152.16) * mm});
            skLineSegment(sketch, "E687", {"start": v(-7.35, -152.16) * mm, "end": v(-7.32, -152.42) * mm});
            skLineSegment(sketch, "E688", {"start": v(-7.32, -152.42) * mm, "end": v(-7.33, -152.72) * mm});
            skLineSegment(sketch, "E689", {"start": v(-7.33, -152.72) * mm, "end": v(-7.41, -152.87) * mm});
            skLineSegment(sketch, "E690", {"start": v(-7.41, -152.87) * mm, "end": v(-7.6, -152.95) * mm});
            skLineSegment(sketch, "E691", {"start": v(-7.6, -152.95) * mm, "end": v(-7.98, -153) * mm});
            skLineSegment(sketch, "E692", {"start": v(-7.98, -153) * mm, "end": v(-8.4, -153.13) * mm});
            skLineSegment(sketch, "E693", {"start": v(-8.4, -153.13) * mm, "end": v(-8.7, -153.36) * mm});
            skLineSegment(sketch, "E694", {"start": v(-8.7, -153.36) * mm, "end": v(-8.87, -153.72) * mm});
            skLineSegment(sketch, "E695", {"start": v(-8.87, -153.72) * mm, "end": v(-8.93, -154.26) * mm});
            skLineSegment(sketch, "E696", {"start": v(-8.93, -154.26) * mm, "end": v(-8.88, -154.73) * mm});
            skLineSegment(sketch, "E697", {"start": v(-8.88, -154.73) * mm, "end": v(-8.73, -155.09) * mm});
            skLineSegment(sketch, "E698", {"start": v(-8.73, -155.09) * mm, "end": v(-8.48, -155.3) * mm});
            skLineSegment(sketch, "E699", {"start": v(-8.48, -155.3) * mm, "end": v(-8.14, -155.39) * mm});
            skLineSegment(sketch, "E700", {"start": v(-8.14, -155.39) * mm, "end": v(-7.69, -155.24) * mm});
            skLineSegment(sketch, "E701", {"start": v(-7.69, -155.24) * mm, "end": v(-7.28, -154.77) * mm});
            skLineSegment(sketch, "E702", {"start": v(-7.33, -153.92) * mm, "end": v(-7.39, -154.3) * mm});
            skLineSegment(sketch, "E703", {"start": v(-7.39, -154.3) * mm, "end": v(-7.55, -154.58) * mm});
            skLineSegment(sketch, "E704", {"start": v(-7.55, -154.58) * mm, "end": v(-7.78, -154.77) * mm});
            skLineSegment(sketch, "E705", {"start": v(-7.78, -154.77) * mm, "end": v(-8.07, -154.83) * mm});
            skLineSegment(sketch, "E706", {"start": v(-8.07, -154.83) * mm, "end": v(-8.26, -154.8) * mm});
            skLineSegment(sketch, "E707", {"start": v(-8.26, -154.8) * mm, "end": v(-8.39, -154.68) * mm});
            skLineSegment(sketch, "E708", {"start": v(-8.39, -154.68) * mm, "end": v(-8.47, -154.48) * mm});
            skLineSegment(sketch, "E709", {"start": v(-8.47, -154.48) * mm, "end": v(-8.5, -154.2) * mm});
            skLineSegment(sketch, "E710", {"start": v(-8.5, -154.2) * mm, "end": v(-8.48, -153.95) * mm});
            skLineSegment(sketch, "E711", {"start": v(-8.48, -153.95) * mm, "end": v(-8.4, -153.77) * mm});
            skLineSegment(sketch, "E712", {"start": v(-8.4, -153.77) * mm, "end": v(-8.08, -153.56) * mm});
            skLineSegment(sketch, "E713", {"start": v(-8.08, -153.56) * mm, "end": v(-7.69, -153.48) * mm});
            skLineSegment(sketch, "E714", {"start": v(-7.69, -153.48) * mm, "end": v(-7.33, -153.3) * mm});
            skLineSegment(sketch, "E715", {"start": v(-7.33, -153.3) * mm, "end": v(-7.33, -153.92) * mm});
            skLineSegment(sketch, "E716", {"start": v(-4.54, -150.63) * mm, "end": v(-4.54, -154.74) * mm});
            skLineSegment(sketch, "E717", {"start": v(-4.54, -154.74) * mm, "end": v(-5.42, -154.74) * mm});
            skLineSegment(sketch, "E718", {"start": v(-5.42, -154.74) * mm, "end": v(-5.42, -155.27) * mm});
            skLineSegment(sketch, "E719", {"start": v(-5.42, -155.27) * mm, "end": v(-3.22, -155.27) * mm});
            skLineSegment(sketch, "E720", {"start": v(-3.22, -155.27) * mm, "end": v(-3.22, -154.74) * mm});
            skLineSegment(sketch, "E721", {"start": v(-3.22, -154.74) * mm, "end": v(-4.1, -154.74) * mm});
            skLineSegment(sketch, "E722", {"start": v(-4.1, -154.74) * mm, "end": v(-4.1, -150.1) * mm});
            skLineSegment(sketch, "E723", {"start": v(-4.1, -150.1) * mm, "end": v(-5.21, -150.1) * mm});
            skLineSegment(sketch, "E724", {"start": v(-5.21, -150.1) * mm, "end": v(-5.21, -150.63) * mm});
            skLineSegment(sketch, "E725", {"start": v(-5.21, -150.63) * mm, "end": v(-4.54, -150.63) * mm});
            skLineSegment(sketch, "E726", {"start": v(1.74, -153.62) * mm, "end": v(1.3, -153.62) * mm});
            skLineSegment(sketch, "E727", {"start": v(1.3, -153.62) * mm, "end": v(1.4, -154.39) * mm});
            skLineSegment(sketch, "E728", {"start": v(1.4, -154.39) * mm, "end": v(1.64, -154.95) * mm});
            skLineSegment(sketch, "E729", {"start": v(1.64, -154.95) * mm, "end": v(2.02, -155.29) * mm});
            skLineSegment(sketch, "E730", {"start": v(2.02, -155.29) * mm, "end": v(2.53, -155.4) * mm});
            skLineSegment(sketch, "E731", {"start": v(2.53, -155.4) * mm, "end": v(3.03, -155.3) * mm});
            skLineSegment(sketch, "E732", {"start": v(3.03, -155.3) * mm, "end": v(3.4, -154.98) * mm});
            skLineSegment(sketch, "E733", {"start": v(3.4, -154.98) * mm, "end": v(3.65, -154.48) * mm});
            skLineSegment(sketch, "E734", {"start": v(3.65, -154.48) * mm, "end": v(3.74, -153.82) * mm});
            skLineSegment(sketch, "E735", {"start": v(3.74, -153.82) * mm, "end": v(3.66, -153.23) * mm});
            skLineSegment(sketch, "E736", {"start": v(3.66, -153.23) * mm, "end": v(3.46, -152.85) * mm});
            skLineSegment(sketch, "E737", {"start": v(3.46, -152.85) * mm, "end": v(3.13, -152.6) * mm});
            skLineSegment(sketch, "E738", {"start": v(3.13, -152.6) * mm, "end": v(2.68, -152.41) * mm});
            skLineSegment(sketch, "E739", {"start": v(2.68, -152.41) * mm, "end": v(2.3, -152.28) * mm});
            skLineSegment(sketch, "E740", {"start": v(2.3, -152.28) * mm, "end": v(2.05, -152.12) * mm});
            skLineSegment(sketch, "E741", {"start": v(2.05, -152.12) * mm, "end": v(1.9, -151.89) * mm});
            skLineSegment(sketch, "E742", {"start": v(1.9, -151.89) * mm, "end": v(1.86, -151.53) * mm});
            skLineSegment(sketch, "E743", {"start": v(1.86, -151.53) * mm, "end": v(1.9, -151.2) * mm});
            skLineSegment(sketch, "E744", {"start": v(1.9, -151.2) * mm, "end": v(2.03, -150.96) * mm});
            skLineSegment(sketch, "E745", {"start": v(2.03, -150.96) * mm, "end": v(2.23, -150.8) * mm});
            skLineSegment(sketch, "E746", {"start": v(2.23, -150.8) * mm, "end": v(2.5, -150.73) * mm});
            skLineSegment(sketch, "E747", {"start": v(2.5, -150.73) * mm, "end": v(2.77, -150.8) * mm});
            skLineSegment(sketch, "E748", {"start": v(2.77, -150.8) * mm, "end": v(2.99, -151) * mm});
            skLineSegment(sketch, "E749", {"start": v(2.99, -151) * mm, "end": v(3.13, -151.32) * mm});
            skLineSegment(sketch, "E750", {"start": v(3.13, -151.32) * mm, "end": v(3.2, -151.76) * mm});
            skLineSegment(sketch, "E751", {"start": v(3.2, -151.76) * mm, "end": v(3.64, -151.76) * mm});
            skLineSegment(sketch, "E752", {"start": v(3.64, -151.76) * mm, "end": v(3.64, -151.75) * mm});
            skLineSegment(sketch, "E753", {"start": v(3.64, -151.75) * mm, "end": v(3.57, -151.07) * mm});
            skLineSegment(sketch, "E754", {"start": v(3.57, -151.07) * mm, "end": v(3.34, -150.57) * mm});
            skLineSegment(sketch, "E755", {"start": v(3.34, -150.57) * mm, "end": v(2.97, -150.25) * mm});
            skLineSegment(sketch, "E756", {"start": v(2.97, -150.25) * mm, "end": v(2.48, -150.14) * mm});
            skLineSegment(sketch, "E757", {"start": v(2.48, -150.14) * mm, "end": v(2.04, -150.25) * mm});
            skLineSegment(sketch, "E758", {"start": v(2.04, -150.25) * mm, "end": v(1.7, -150.55) * mm});
            skLineSegment(sketch, "E759", {"start": v(1.7, -150.55) * mm, "end": v(1.48, -151.02) * mm});
            skLineSegment(sketch, "E760", {"start": v(1.48, -151.02) * mm, "end": v(1.4, -151.63) * mm});
            skLineSegment(sketch, "E761", {"start": v(1.4, -151.63) * mm, "end": v(1.46, -152.17) * mm});
            skLineSegment(sketch, "E762", {"start": v(1.46, -152.17) * mm, "end": v(1.65, -152.53) * mm});
            skLineSegment(sketch, "E763", {"start": v(1.65, -152.53) * mm, "end": v(1.94, -152.78) * mm});
            skLineSegment(sketch, "E764", {"start": v(1.94, -152.78) * mm, "end": v(2.35, -152.97) * mm});
            skLineSegment(sketch, "E765", {"start": v(2.35, -152.97) * mm, "end": v(2.74, -153.13) * mm});
            skLineSegment(sketch, "E766", {"start": v(2.74, -153.13) * mm, "end": v(3.04, -153.3) * mm});
            skLineSegment(sketch, "E767", {"start": v(3.04, -153.3) * mm, "end": v(3.22, -153.52) * mm});
            skLineSegment(sketch, "E768", {"start": v(3.22, -153.52) * mm, "end": v(3.29, -153.9) * mm});
            skLineSegment(sketch, "E769", {"start": v(3.29, -153.9) * mm, "end": v(3.23, -154.28) * mm});
            skLineSegment(sketch, "E770", {"start": v(3.23, -154.28) * mm, "end": v(3.08, -154.57) * mm});
            skLineSegment(sketch, "E771", {"start": v(3.08, -154.57) * mm, "end": v(2.85, -154.75) * mm});
            skLineSegment(sketch, "E772", {"start": v(2.85, -154.75) * mm, "end": v(2.55, -154.8) * mm});
            skLineSegment(sketch, "E773", {"start": v(2.55, -154.8) * mm, "end": v(2.21, -154.72) * mm});
            skLineSegment(sketch, "E774", {"start": v(2.21, -154.72) * mm, "end": v(1.96, -154.5) * mm});
            skLineSegment(sketch, "E775", {"start": v(1.96, -154.5) * mm, "end": v(1.8, -154.12) * mm});
            skLineSegment(sketch, "E776", {"start": v(1.8, -154.12) * mm, "end": v(1.74, -153.62) * mm});
            skLineSegment(sketch, "E777", {"start": v(5.53, -152.07) * mm, "end": v(5.53, -154.01) * mm});
            skLineSegment(sketch, "E778", {"start": v(5.53, -154.01) * mm, "end": v(5.56, -154.64) * mm});
            skLineSegment(sketch, "E779", {"start": v(5.56, -154.64) * mm, "end": v(5.7, -155.07) * mm});
            skLineSegment(sketch, "E780", {"start": v(5.7, -155.07) * mm, "end": v(5.97, -155.32) * mm});
            skLineSegment(sketch, "E781", {"start": v(5.97, -155.32) * mm, "end": v(6.44, -155.4) * mm});
            skLineSegment(sketch, "E782", {"start": v(6.44, -155.4) * mm, "end": v(6.95, -155.37) * mm});
            skLineSegment(sketch, "E783", {"start": v(6.95, -155.37) * mm, "end": v(6.95, -154.83) * mm});
            skLineSegment(sketch, "E784", {"start": v(6.95, -154.83) * mm, "end": v(6.57, -154.87) * mm});
            skLineSegment(sketch, "E785", {"start": v(6.57, -154.87) * mm, "end": v(6.24, -154.81) * mm});
            skLineSegment(sketch, "E786", {"start": v(6.24, -154.81) * mm, "end": v(6.06, -154.63) * mm});
            skLineSegment(sketch, "E787", {"start": v(6.06, -154.63) * mm, "end": v(5.98, -154.33) * mm});
            skLineSegment(sketch, "E788", {"start": v(5.98, -154.33) * mm, "end": v(5.96, -153.9) * mm});
            skLineSegment(sketch, "E789", {"start": v(5.96, -153.9) * mm, "end": v(5.96, -152.07) * mm});
            skLineSegment(sketch, "E790", {"start": v(5.96, -152.07) * mm, "end": v(6.95, -152.07) * mm});
            skLineSegment(sketch, "E791", {"start": v(6.95, -152.07) * mm, "end": v(6.95, -151.53) * mm});
            skLineSegment(sketch, "E792", {"start": v(6.95, -151.53) * mm, "end": v(5.96, -151.53) * mm});
            skLineSegment(sketch, "E793", {"start": v(5.96, -151.53) * mm, "end": v(5.96, -150.4) * mm});
            skLineSegment(sketch, "E794", {"start": v(5.96, -150.4) * mm, "end": v(5.53, -150.4) * mm});
            skLineSegment(sketch, "E795", {"start": v(5.53, -150.4) * mm, "end": v(5.53, -151.53) * mm});
            skLineSegment(sketch, "E796", {"start": v(5.53, -151.53) * mm, "end": v(4.79, -151.53) * mm});
            skLineSegment(sketch, "E797", {"start": v(4.79, -151.53) * mm, "end": v(4.79, -152.07) * mm});
            skLineSegment(sketch, "E798", {"start": v(4.79, -152.07) * mm, "end": v(5.53, -152.07) * mm});
            skLineSegment(sketch, "E799", {"start": v(9.97, -154.77) * mm, "end": v(9.97, -154.79) * mm});
            skLineSegment(sketch, "E800", {"start": v(9.97, -154.79) * mm, "end": v(9.99, -155.03) * mm});
            skLineSegment(sketch, "E801", {"start": v(9.99, -155.03) * mm, "end": v(10.06, -155.2) * mm});
            skLineSegment(sketch, "E802", {"start": v(10.06, -155.2) * mm, "end": v(10.37, -155.34) * mm});
            skLineSegment(sketch, "E803", {"start": v(10.37, -155.34) * mm, "end": v(10.61, -155.29) * mm});
            skLineSegment(sketch, "E804", {"start": v(10.61, -155.29) * mm, "end": v(10.61, -154.8) * mm});
            skLineSegment(sketch, "E805", {"start": v(10.61, -154.8) * mm, "end": v(10.5, -154.82) * mm});
            skLineSegment(sketch, "E806", {"start": v(10.5, -154.82) * mm, "end": v(10.37, -154.72) * mm});
            skLineSegment(sketch, "E807", {"start": v(10.37, -154.72) * mm, "end": v(10.35, -154.44) * mm});
            skLineSegment(sketch, "E808", {"start": v(10.35, -154.44) * mm, "end": v(10.35, -152.43) * mm});
            skLineSegment(sketch, "E809", {"start": v(10.35, -152.43) * mm, "end": v(10.29, -151.92) * mm});
            skLineSegment(sketch, "E810", {"start": v(10.29, -151.92) * mm, "end": v(10.12, -151.56) * mm});
            skLineSegment(sketch, "E811", {"start": v(10.12, -151.56) * mm, "end": v(9.82, -151.35) * mm});
            skLineSegment(sketch, "E812", {"start": v(9.82, -151.35) * mm, "end": v(9.4, -151.27) * mm});
            skLineSegment(sketch, "E813", {"start": v(9.4, -151.27) * mm, "end": v(8.99, -151.35) * mm});
            skLineSegment(sketch, "E814", {"start": v(8.99, -151.35) * mm, "end": v(8.68, -151.6) * mm});
            skLineSegment(sketch, "E815", {"start": v(8.68, -151.6) * mm, "end": v(8.5, -151.98) * mm});
            skLineSegment(sketch, "E816", {"start": v(8.5, -151.98) * mm, "end": v(8.43, -152.48) * mm});
            skLineSegment(sketch, "E817", {"start": v(8.43, -152.48) * mm, "end": v(8.43, -152.53) * mm});
            skLineSegment(sketch, "E818", {"start": v(8.43, -152.53) * mm, "end": v(8.81, -152.53) * mm});
            skLineSegment(sketch, "E819", {"start": v(8.81, -152.53) * mm, "end": v(8.85, -152.22) * mm});
            skLineSegment(sketch, "E820", {"start": v(8.85, -152.22) * mm, "end": v(8.96, -152) * mm});
            skLineSegment(sketch, "E821", {"start": v(8.96, -152) * mm, "end": v(9.13, -151.88) * mm});
            skLineSegment(sketch, "E822", {"start": v(9.13, -151.88) * mm, "end": v(9.38, -151.83) * mm});
            skLineSegment(sketch, "E823", {"start": v(9.38, -151.83) * mm, "end": v(9.62, -151.86) * mm});
            skLineSegment(sketch, "E824", {"start": v(9.62, -151.86) * mm, "end": v(9.8, -151.97) * mm});
            skLineSegment(sketch, "E825", {"start": v(9.8, -151.97) * mm, "end": v(9.9, -152.16) * mm});
            skLineSegment(sketch, "E826", {"start": v(9.9, -152.16) * mm, "end": v(9.93, -152.42) * mm});
            skLineSegment(sketch, "E827", {"start": v(9.93, -152.42) * mm, "end": v(9.91, -152.72) * mm});
            skLineSegment(sketch, "E828", {"start": v(9.91, -152.72) * mm, "end": v(9.83, -152.87) * mm});
            skLineSegment(sketch, "E829", {"start": v(9.83, -152.87) * mm, "end": v(9.64, -152.95) * mm});
            skLineSegment(sketch, "E830", {"start": v(9.64, -152.95) * mm, "end": v(9.27, -153) * mm});
            skLineSegment(sketch, "E831", {"start": v(9.27, -153) * mm, "end": v(8.85, -153.13) * mm});
            skLineSegment(sketch, "E832", {"start": v(8.85, -153.13) * mm, "end": v(8.55, -153.36) * mm});
            skLineSegment(sketch, "E833", {"start": v(8.55, -153.36) * mm, "end": v(8.37, -153.72) * mm});
            skLineSegment(sketch, "E834", {"start": v(8.37, -153.72) * mm, "end": v(8.32, -154.26) * mm});
            skLineSegment(sketch, "E835", {"start": v(8.32, -154.26) * mm, "end": v(8.37, -154.73) * mm});
            skLineSegment(sketch, "E836", {"start": v(8.37, -154.73) * mm, "end": v(8.52, -155.09) * mm});
            skLineSegment(sketch, "E837", {"start": v(8.52, -155.09) * mm, "end": v(8.77, -155.3) * mm});
            skLineSegment(sketch, "E838", {"start": v(8.77, -155.3) * mm, "end": v(9.1, -155.39) * mm});
            skLineSegment(sketch, "E839", {"start": v(9.1, -155.39) * mm, "end": v(9.56, -155.24) * mm});
            skLineSegment(sketch, "E840", {"start": v(9.56, -155.24) * mm, "end": v(9.97, -154.77) * mm});
            skLineSegment(sketch, "E841", {"start": v(9.92, -153.92) * mm, "end": v(9.86, -154.3) * mm});
            skLineSegment(sketch, "E842", {"start": v(9.86, -154.3) * mm, "end": v(9.7, -154.58) * mm});
            skLineSegment(sketch, "E843", {"start": v(9.7, -154.58) * mm, "end": v(9.47, -154.77) * mm});
            skLineSegment(sketch, "E844", {"start": v(9.47, -154.77) * mm, "end": v(9.18, -154.83) * mm});
            skLineSegment(sketch, "E845", {"start": v(9.18, -154.83) * mm, "end": v(9, -154.8) * mm});
            skLineSegment(sketch, "E846", {"start": v(9, -154.8) * mm, "end": v(8.86, -154.68) * mm});
            skLineSegment(sketch, "E847", {"start": v(8.86, -154.68) * mm, "end": v(8.77, -154.48) * mm});
            skLineSegment(sketch, "E848", {"start": v(8.77, -154.48) * mm, "end": v(8.75, -154.2) * mm});
            skLineSegment(sketch, "E849", {"start": v(8.75, -154.2) * mm, "end": v(8.77, -153.95) * mm});
            skLineSegment(sketch, "E850", {"start": v(8.77, -153.95) * mm, "end": v(8.85, -153.77) * mm});
            skLineSegment(sketch, "E851", {"start": v(8.85, -153.77) * mm, "end": v(9.16, -153.56) * mm});
            skLineSegment(sketch, "E852", {"start": v(9.16, -153.56) * mm, "end": v(9.56, -153.48) * mm});
            skLineSegment(sketch, "E853", {"start": v(9.56, -153.48) * mm, "end": v(9.92, -153.3) * mm});
            skLineSegment(sketch, "E854", {"start": v(9.92, -153.3) * mm, "end": v(9.92, -153.92) * mm});
            skLineSegment(sketch, "E855", {"start": v(11.85, -155.27) * mm, "end": v(12.28, -155.27) * mm});
            skLineSegment(sketch, "E856", {"start": v(12.28, -155.27) * mm, "end": v(12.28, -153.04) * mm});
            skLineSegment(sketch, "E857", {"start": v(12.28, -153.04) * mm, "end": v(12.33, -152.53) * mm});
            skLineSegment(sketch, "E858", {"start": v(12.33, -152.53) * mm, "end": v(12.47, -152.15) * mm});
            skLineSegment(sketch, "E859", {"start": v(12.47, -152.15) * mm, "end": v(12.69, -151.92) * mm});
            skLineSegment(sketch, "E860", {"start": v(12.69, -151.92) * mm, "end": v(12.98, -151.84) * mm});
            skLineSegment(sketch, "E861", {"start": v(12.98, -151.84) * mm, "end": v(13.22, -151.9) * mm});
            skLineSegment(sketch, "E862", {"start": v(13.22, -151.9) * mm, "end": v(13.37, -152.1) * mm});
            skLineSegment(sketch, "E863", {"start": v(13.37, -152.1) * mm, "end": v(13.44, -152.43) * mm});
            skLineSegment(sketch, "E864", {"start": v(13.44, -152.43) * mm, "end": v(13.46, -152.86) * mm});
            skLineSegment(sketch, "E865", {"start": v(13.46, -152.86) * mm, "end": v(13.46, -155.27) * mm});
            skLineSegment(sketch, "E866", {"start": v(13.46, -155.27) * mm, "end": v(13.9, -155.27) * mm});
            skLineSegment(sketch, "E867", {"start": v(13.9, -155.27) * mm, "end": v(13.9, -152.73) * mm});
            skLineSegment(sketch, "E868", {"start": v(13.9, -152.73) * mm, "end": v(13.88, -152.22) * mm});
            skLineSegment(sketch, "E869", {"start": v(13.88, -152.22) * mm, "end": v(13.79, -151.8) * mm});
            skLineSegment(sketch, "E870", {"start": v(13.79, -151.8) * mm, "end": v(13.5, -151.4) * mm});
            skLineSegment(sketch, "E871", {"start": v(13.5, -151.4) * mm, "end": v(13.05, -151.27) * mm});
            skLineSegment(sketch, "E872", {"start": v(13.05, -151.27) * mm, "end": v(12.8, -151.32) * mm});
            skLineSegment(sketch, "E873", {"start": v(12.8, -151.32) * mm, "end": v(12.6, -151.45) * mm});
            skLineSegment(sketch, "E874", {"start": v(12.6, -151.45) * mm, "end": v(12.42, -151.67) * mm});
            skLineSegment(sketch, "E875", {"start": v(12.42, -151.67) * mm, "end": v(12.28, -151.97) * mm});
            skLineSegment(sketch, "E876", {"start": v(12.28, -151.97) * mm, "end": v(12.28, -150.1) * mm});
            skLineSegment(sketch, "E877", {"start": v(12.28, -150.1) * mm, "end": v(11.85, -150.1) * mm});
            skLineSegment(sketch, "E878", {"start": v(11.85, -150.1) * mm, "end": v(11.85, -155.27) * mm});
            skLineSegment(sketch, "E879", {"start": v(16.16, -150.63) * mm, "end": v(16.16, -154.74) * mm});
            skLineSegment(sketch, "E880", {"start": v(16.16, -154.74) * mm, "end": v(15.27, -154.74) * mm});
            skLineSegment(sketch, "E881", {"start": v(15.27, -154.74) * mm, "end": v(15.27, -155.27) * mm});
            skLineSegment(sketch, "E882", {"start": v(15.27, -155.27) * mm, "end": v(17.47, -155.27) * mm});
            skLineSegment(sketch, "E883", {"start": v(17.47, -155.27) * mm, "end": v(17.47, -154.74) * mm});
            skLineSegment(sketch, "E884", {"start": v(17.47, -154.74) * mm, "end": v(16.59, -154.74) * mm});
            skLineSegment(sketch, "E885", {"start": v(16.59, -154.74) * mm, "end": v(16.59, -150.1) * mm});
            skLineSegment(sketch, "E886", {"start": v(16.59, -150.1) * mm, "end": v(15.48, -150.1) * mm});
            skLineSegment(sketch, "E887", {"start": v(15.48, -150.1) * mm, "end": v(15.48, -150.63) * mm});
            skLineSegment(sketch, "E888", {"start": v(15.48, -150.63) * mm, "end": v(16.16, -150.63) * mm});
            skLineSegment(sketch, "E889", {"start": v(22.07, -151.51) * mm, "end": v(23.88, -152.7) * mm});
            skLineSegment(sketch, "E890", {"start": v(23.88, -152.7) * mm, "end": v(22.07, -153.89) * mm});
            skLineSegment(sketch, "E891", {"start": v(22.07, -153.89) * mm, "end": v(22.07, -154.47) * mm});
            skLineSegment(sketch, "E892", {"start": v(22.07, -154.47) * mm, "end": v(24.35, -152.93) * mm});
            skLineSegment(sketch, "E893", {"start": v(24.35, -152.93) * mm, "end": v(24.35, -152.48) * mm});
            skLineSegment(sketch, "E894", {"start": v(24.35, -152.48) * mm, "end": v(22.07, -150.94) * mm});
            skLineSegment(sketch, "E895", {"start": v(22.07, -150.94) * mm, "end": v(22.07, -151.51) * mm});
            skLineSegment(sketch, "E896", {"start": v(25.52, -153.17) * mm, "end": v(25.52, -153.66) * mm});
            skLineSegment(sketch, "E897", {"start": v(25.52, -153.66) * mm, "end": v(27.8, -153.66) * mm});
            skLineSegment(sketch, "E898", {"start": v(27.8, -153.66) * mm, "end": v(27.8, -153.17) * mm});
            skLineSegment(sketch, "E899", {"start": v(27.8, -153.17) * mm, "end": v(25.52, -153.17) * mm});
            skLineSegment(sketch, "E900", {"start": v(25.52, -151.77) * mm, "end": v(25.52, -152.27) * mm});
            skLineSegment(sketch, "E901", {"start": v(25.52, -152.27) * mm, "end": v(27.8, -152.27) * mm});
            skLineSegment(sketch, "E902", {"start": v(27.8, -152.27) * mm, "end": v(27.8, -151.77) * mm});
            skLineSegment(sketch, "E903", {"start": v(27.8, -151.77) * mm, "end": v(25.52, -151.77) * mm});
            skLineSegment(sketch, "E904", {"start": v(32.33, -153.7) * mm, "end": v(32.33, -153.75) * mm});
            skLineSegment(sketch, "E905", {"start": v(32.33, -153.75) * mm, "end": v(32.4, -154.44) * mm});
            skLineSegment(sketch, "E906", {"start": v(32.4, -154.44) * mm, "end": v(32.64, -154.96) * mm});
            skLineSegment(sketch, "E907", {"start": v(32.64, -154.96) * mm, "end": v(33, -155.3) * mm});
            skLineSegment(sketch, "E908", {"start": v(33, -155.3) * mm, "end": v(33.48, -155.42) * mm});
            skLineSegment(sketch, "E909", {"start": v(33.48, -155.42) * mm, "end": v(33.99, -155.3) * mm});
            skLineSegment(sketch, "E910", {"start": v(33.99, -155.3) * mm, "end": v(34.37, -154.98) * mm});
            skLineSegment(sketch, "E911", {"start": v(34.37, -154.98) * mm, "end": v(34.61, -154.47) * mm});
            skLineSegment(sketch, "E912", {"start": v(34.61, -154.47) * mm, "end": v(34.7, -153.82) * mm});
            skLineSegment(sketch, "E913", {"start": v(34.7, -153.82) * mm, "end": v(34.66, -153.4) * mm});
            skLineSegment(sketch, "E914", {"start": v(34.66, -153.4) * mm, "end": v(34.56, -153.05) * mm});
            skLineSegment(sketch, "E915", {"start": v(34.56, -153.05) * mm, "end": v(34.38, -152.79) * mm});
            skLineSegment(sketch, "E916", {"start": v(34.38, -152.79) * mm, "end": v(34.14, -152.6) * mm});
            skLineSegment(sketch, "E917", {"start": v(34.14, -152.6) * mm, "end": v(34.46, -152.2) * mm});
            skLineSegment(sketch, "E918", {"start": v(34.46, -152.2) * mm, "end": v(34.58, -151.58) * mm});
            skLineSegment(sketch, "E919", {"start": v(34.58, -151.58) * mm, "end": v(34.5, -151.02) * mm});
            skLineSegment(sketch, "E920", {"start": v(34.5, -151.02) * mm, "end": v(34.3, -150.6) * mm});
            skLineSegment(sketch, "E921", {"start": v(34.3, -150.6) * mm, "end": v(33.95, -150.33) * mm});
            skLineSegment(sketch, "E922", {"start": v(33.95, -150.33) * mm, "end": v(33.48, -150.24) * mm});
            skLineSegment(sketch, "E923", {"start": v(33.48, -150.24) * mm, "end": v(33.04, -150.35) * mm});
            skLineSegment(sketch, "E924", {"start": v(33.04, -150.35) * mm, "end": v(32.7, -150.67) * mm});
            skLineSegment(sketch, "E925", {"start": v(32.7, -150.67) * mm, "end": v(32.48, -151.17) * mm});
            skLineSegment(sketch, "E926", {"start": v(32.48, -151.17) * mm, "end": v(32.4, -151.84) * mm});
            skLineSegment(sketch, "E927", {"start": v(32.4, -151.84) * mm, "end": v(32.4, -151.9) * mm});
            skLineSegment(sketch, "E928", {"start": v(32.4, -151.9) * mm, "end": v(32.84, -151.9) * mm});
            skLineSegment(sketch, "E929", {"start": v(32.84, -151.9) * mm, "end": v(32.88, -151.43) * mm});
            skLineSegment(sketch, "E930", {"start": v(32.88, -151.43) * mm, "end": v(33, -151.1) * mm});
            skLineSegment(sketch, "E931", {"start": v(33, -151.1) * mm, "end": v(33.21, -150.9) * mm});
            skLineSegment(sketch, "E932", {"start": v(33.21, -150.9) * mm, "end": v(33.5, -150.83) * mm});
            skLineSegment(sketch, "E933", {"start": v(33.5, -150.83) * mm, "end": v(33.76, -150.88) * mm});
            skLineSegment(sketch, "E934", {"start": v(33.76, -150.88) * mm, "end": v(33.94, -151.04) * mm});
            skLineSegment(sketch, "E935", {"start": v(33.94, -151.04) * mm, "end": v(34.06, -151.28) * mm});
            skLineSegment(sketch, "E936", {"start": v(34.06, -151.28) * mm, "end": v(34.1, -151.61) * mm});
            skLineSegment(sketch, "E937", {"start": v(34.1, -151.61) * mm, "end": v(34.06, -151.97) * mm});
            skLineSegment(sketch, "E938", {"start": v(34.06, -151.97) * mm, "end": v(33.94, -152.2) * mm});
            skLineSegment(sketch, "E939", {"start": v(33.94, -152.2) * mm, "end": v(33.73, -152.35) * mm});
            skLineSegment(sketch, "E940", {"start": v(33.73, -152.35) * mm, "end": v(33.45, -152.4) * mm});
            skLineSegment(sketch, "E941", {"start": v(33.45, -152.4) * mm, "end": v(33.26, -152.38) * mm});
            skLineSegment(sketch, "E942", {"start": v(33.26, -152.38) * mm, "end": v(33.26, -152.95) * mm});
            skLineSegment(sketch, "E943", {"start": v(33.26, -152.95) * mm, "end": v(33.5, -152.94) * mm});
            skLineSegment(sketch, "E944", {"start": v(33.5, -152.94) * mm, "end": v(33.81, -153) * mm});
            skLineSegment(sketch, "E945", {"start": v(33.81, -153) * mm, "end": v(34.04, -153.18) * mm});
            skLineSegment(sketch, "E946", {"start": v(34.04, -153.18) * mm, "end": v(34.18, -153.46) * mm});
            skLineSegment(sketch, "E947", {"start": v(34.18, -153.46) * mm, "end": v(34.23, -153.82) * mm});
            skLineSegment(sketch, "E948", {"start": v(34.23, -153.82) * mm, "end": v(34.17, -154.24) * mm});
            skLineSegment(sketch, "E949", {"start": v(34.17, -154.24) * mm, "end": v(34.03, -154.55) * mm});
            skLineSegment(sketch, "E950", {"start": v(34.03, -154.55) * mm, "end": v(33.8, -154.75) * mm});
            skLineSegment(sketch, "E951", {"start": v(33.8, -154.75) * mm, "end": v(33.5, -154.81) * mm});
            skLineSegment(sketch, "E952", {"start": v(33.5, -154.81) * mm, "end": v(33.2, -154.74) * mm});
            skLineSegment(sketch, "E953", {"start": v(33.2, -154.74) * mm, "end": v(32.97, -154.52) * mm});
            skLineSegment(sketch, "E954", {"start": v(32.97, -154.52) * mm, "end": v(32.83, -154.18) * mm});
            skLineSegment(sketch, "E955", {"start": v(32.83, -154.18) * mm, "end": v(32.78, -153.7) * mm});
            skLineSegment(sketch, "E956", {"start": v(32.78, -153.7) * mm, "end": v(32.33, -153.7) * mm});
            skLineSegment(sketch, "E957", {"start": v(35.83, -152.83) * mm, "end": v(35.9, -153.96) * mm});
            skLineSegment(sketch, "E958", {"start": v(35.9, -153.96) * mm, "end": v(36.13, -154.77) * mm});
            skLineSegment(sketch, "E959", {"start": v(36.13, -154.77) * mm, "end": v(36.5, -155.26) * mm});
            skLineSegment(sketch, "E960", {"start": v(36.5, -155.26) * mm, "end": v(37.01, -155.42) * mm});
            skLineSegment(sketch, "E961", {"start": v(37.01, -155.42) * mm, "end": v(37.52, -155.26) * mm});
            skLineSegment(sketch, "E962", {"start": v(37.52, -155.26) * mm, "end": v(37.88, -154.77) * mm});
            skLineSegment(sketch, "E963", {"start": v(37.88, -154.77) * mm, "end": v(38.1, -153.96) * mm});
            skLineSegment(sketch, "E964", {"start": v(38.1, -153.96) * mm, "end": v(38.19, -152.83) * mm});
            skLineSegment(sketch, "E965", {"start": v(38.19, -152.83) * mm, "end": v(38.1, -151.7) * mm});
            skLineSegment(sketch, "E966", {"start": v(38.1, -151.7) * mm, "end": v(38.02, -151.26) * mm});
            skLineSegment(sketch, "E967", {"start": v(38.02, -151.26) * mm, "end": v(37.88, -150.9) * mm});
            skLineSegment(sketch, "E968", {"start": v(37.88, -150.9) * mm, "end": v(37.52, -150.4) * mm});
            skLineSegment(sketch, "E969", {"start": v(37.52, -150.4) * mm, "end": v(37.01, -150.24) * mm});
            skLineSegment(sketch, "E970", {"start": v(37.01, -150.24) * mm, "end": v(36.5, -150.4) * mm});
            skLineSegment(sketch, "E971", {"start": v(36.5, -150.4) * mm, "end": v(36.13, -150.9) * mm});
            skLineSegment(sketch, "E972", {"start": v(36.13, -150.9) * mm, "end": v(35.9, -151.7) * mm});
            skLineSegment(sketch, "E973", {"start": v(35.9, -151.7) * mm, "end": v(35.83, -152.83) * mm});
            skLineSegment(sketch, "E974", {"start": v(36.3, -152.83) * mm, "end": v(36.34, -151.96) * mm});
            skLineSegment(sketch, "E975", {"start": v(36.34, -151.96) * mm, "end": v(36.46, -151.33) * mm});
            skLineSegment(sketch, "E976", {"start": v(36.46, -151.33) * mm, "end": v(36.68, -150.96) * mm});
            skLineSegment(sketch, "E977", {"start": v(36.68, -150.96) * mm, "end": v(37.01, -150.83) * mm});
            skLineSegment(sketch, "E978", {"start": v(37.01, -150.83) * mm, "end": v(37.33, -150.96) * mm});
            skLineSegment(sketch, "E979", {"start": v(37.33, -150.96) * mm, "end": v(37.55, -151.33) * mm});
            skLineSegment(sketch, "E980", {"start": v(37.55, -151.33) * mm, "end": v(37.68, -151.96) * mm});
            skLineSegment(sketch, "E981", {"start": v(37.68, -151.96) * mm, "end": v(37.72, -152.83) * mm});
            skLineSegment(sketch, "E982", {"start": v(37.72, -152.83) * mm, "end": v(37.68, -153.7) * mm});
            skLineSegment(sketch, "E983", {"start": v(37.68, -153.7) * mm, "end": v(37.55, -154.34) * mm});
            skLineSegment(sketch, "E984", {"start": v(37.55, -154.34) * mm, "end": v(37.33, -154.7) * mm});
            skLineSegment(sketch, "E985", {"start": v(37.33, -154.7) * mm, "end": v(37.01, -154.83) * mm});
            skLineSegment(sketch, "E986", {"start": v(37.01, -154.83) * mm, "end": v(36.68, -154.7) * mm});
            skLineSegment(sketch, "E987", {"start": v(36.68, -154.7) * mm, "end": v(36.46, -154.34) * mm});
            skLineSegment(sketch, "E988", {"start": v(36.46, -154.34) * mm, "end": v(36.34, -153.7) * mm});
            skLineSegment(sketch, "E989", {"start": v(36.34, -153.7) * mm, "end": v(36.3, -152.83) * mm});
            skLineSegment(sketch, "E990", {"start": v(39.28, -152.83) * mm, "end": v(39.35, -153.96) * mm});
            skLineSegment(sketch, "E991", {"start": v(39.35, -153.96) * mm, "end": v(39.58, -154.77) * mm});
            skLineSegment(sketch, "E992", {"start": v(39.58, -154.77) * mm, "end": v(39.95, -155.26) * mm});
            skLineSegment(sketch, "E993", {"start": v(39.95, -155.26) * mm, "end": v(40.46, -155.42) * mm});
            skLineSegment(sketch, "E994", {"start": v(40.46, -155.42) * mm, "end": v(40.96, -155.26) * mm});
            skLineSegment(sketch, "E995", {"start": v(40.96, -155.26) * mm, "end": v(41.33, -154.77) * mm});
            skLineSegment(sketch, "E996", {"start": v(41.33, -154.77) * mm, "end": v(41.56, -153.96) * mm});
            skLineSegment(sketch, "E997", {"start": v(41.56, -153.96) * mm, "end": v(41.64, -152.83) * mm});
            skLineSegment(sketch, "E998", {"start": v(41.64, -152.83) * mm, "end": v(41.56, -151.7) * mm});
            skLineSegment(sketch, "E999", {"start": v(41.56, -151.7) * mm, "end": v(41.46, -151.26) * mm});
            skLineSegment(sketch, "E1000", {"start": v(41.46, -151.26) * mm, "end": v(41.33, -150.9) * mm});
            skLineSegment(sketch, "E1001", {"start": v(41.33, -150.9) * mm, "end": v(40.96, -150.4) * mm});
            skLineSegment(sketch, "E1002", {"start": v(40.96, -150.4) * mm, "end": v(40.46, -150.24) * mm});
            skLineSegment(sketch, "E1003", {"start": v(40.46, -150.24) * mm, "end": v(39.95, -150.4) * mm});
            skLineSegment(sketch, "E1004", {"start": v(39.95, -150.4) * mm, "end": v(39.58, -150.9) * mm});
            skLineSegment(sketch, "E1005", {"start": v(39.58, -150.9) * mm, "end": v(39.35, -151.7) * mm});
            skLineSegment(sketch, "E1006", {"start": v(39.35, -151.7) * mm, "end": v(39.28, -152.83) * mm});
            skLineSegment(sketch, "E1007", {"start": v(39.75, -152.83) * mm, "end": v(39.79, -151.96) * mm});
            skLineSegment(sketch, "E1008", {"start": v(39.79, -151.96) * mm, "end": v(39.91, -151.33) * mm});
            skLineSegment(sketch, "E1009", {"start": v(39.91, -151.33) * mm, "end": v(40.13, -150.96) * mm});
            skLineSegment(sketch, "E1010", {"start": v(40.13, -150.96) * mm, "end": v(40.46, -150.83) * mm});
            skLineSegment(sketch, "E1011", {"start": v(40.46, -150.83) * mm, "end": v(40.78, -150.96) * mm});
            skLineSegment(sketch, "E1012", {"start": v(40.78, -150.96) * mm, "end": v(41, -151.33) * mm});
            skLineSegment(sketch, "E1013", {"start": v(41, -151.33) * mm, "end": v(41.13, -151.96) * mm});
            skLineSegment(sketch, "E1014", {"start": v(41.13, -151.96) * mm, "end": v(41.17, -152.83) * mm});
            skLineSegment(sketch, "E1015", {"start": v(41.17, -152.83) * mm, "end": v(41.13, -153.7) * mm});
            skLineSegment(sketch, "E1016", {"start": v(41.13, -153.7) * mm, "end": v(41, -154.34) * mm});
            skLineSegment(sketch, "E1017", {"start": v(41, -154.34) * mm, "end": v(40.78, -154.7) * mm});
            skLineSegment(sketch, "E1018", {"start": v(40.78, -154.7) * mm, "end": v(40.46, -154.83) * mm});
            skLineSegment(sketch, "E1019", {"start": v(40.46, -154.83) * mm, "end": v(40.13, -154.7) * mm});
            skLineSegment(sketch, "E1020", {"start": v(40.13, -154.7) * mm, "end": v(39.91, -154.34) * mm});
            skLineSegment(sketch, "E1021", {"start": v(39.91, -154.34) * mm, "end": v(39.79, -153.7) * mm});
            skLineSegment(sketch, "E1022", {"start": v(39.79, -153.7) * mm, "end": v(39.75, -152.83) * mm});
            skLineSegment(sketch, "E1023", {"start": v(42.8, -155.27) * mm, "end": v(43.2, -155.27) * mm});
            skLineSegment(sketch, "E1024", {"start": v(43.2, -155.27) * mm, "end": v(43.2, -151.17) * mm});
            skLineSegment(sketch, "E1025", {"start": v(43.2, -151.17) * mm, "end": v(44.5, -155.27) * mm});
            skLineSegment(sketch, "E1026", {"start": v(44.5, -155.27) * mm, "end": v(45.03, -155.27) * mm});
            skLineSegment(sketch, "E1027", {"start": v(45.03, -155.27) * mm, "end": v(45.03, -150.27) * mm});
            skLineSegment(sketch, "E1028", {"start": v(45.03, -150.27) * mm, "end": v(44.61, -150.27) * mm});
            skLineSegment(sketch, "E1029", {"start": v(44.61, -150.27) * mm, "end": v(44.61, -154.37) * mm});
            skLineSegment(sketch, "E1030", {"start": v(44.61, -154.37) * mm, "end": v(43.33, -150.27) * mm});
            skLineSegment(sketch, "E1031", {"start": v(43.33, -150.27) * mm, "end": v(42.8, -150.27) * mm});
            skLineSegment(sketch, "E1032", {"start": v(42.8, -150.27) * mm, "end": v(42.8, -155.27) * mm});
            skLineSegment(sketch, "E1033", {"start": v(46.6, -155.94) * mm, "end": v(46.93, -155.94) * mm});
            skLineSegment(sketch, "E1034", {"start": v(46.93, -155.94) * mm, "end": v(48.12, -150.14) * mm});
            skLineSegment(sketch, "E1035", {"start": v(48.12, -150.14) * mm, "end": v(47.78, -150.14) * mm});
            skLineSegment(sketch, "E1036", {"start": v(47.78, -150.14) * mm, "end": v(46.6, -155.94) * mm});
            skLineSegment(sketch, "E1037", {"start": v(49.62, -155.27) * mm, "end": v(50.02, -155.27) * mm});
            skLineSegment(sketch, "E1038", {"start": v(50.02, -155.27) * mm, "end": v(50.02, -152.69) * mm});
            skLineSegment(sketch, "E1039", {"start": v(50.02, -152.69) * mm, "end": v(50.04, -152.3) * mm});
            skLineSegment(sketch, "E1040", {"start": v(50.04, -152.3) * mm, "end": v(50.12, -152.02) * mm});
            skLineSegment(sketch, "E1041", {"start": v(50.12, -152.02) * mm, "end": v(50.23, -151.85) * mm});
            skLineSegment(sketch, "E1042", {"start": v(50.23, -151.85) * mm, "end": v(50.38, -151.79) * mm});
            skLineSegment(sketch, "E1043", {"start": v(50.38, -151.79) * mm, "end": v(50.5, -151.84) * mm});
            skLineSegment(sketch, "E1044", {"start": v(50.5, -151.84) * mm, "end": v(50.57, -151.99) * mm});
            skLineSegment(sketch, "E1045", {"start": v(50.57, -151.99) * mm, "end": v(50.61, -152.23) * mm});
            skLineSegment(sketch, "E1046", {"start": v(50.61, -152.23) * mm, "end": v(50.63, -152.56) * mm});
            skLineSegment(sketch, "E1047", {"start": v(50.63, -152.56) * mm, "end": v(50.63, -155.27) * mm});
            skLineSegment(sketch, "E1048", {"start": v(50.63, -155.27) * mm, "end": v(51, -155.27) * mm});
            skLineSegment(sketch, "E1049", {"start": v(51, -155.27) * mm, "end": v(51, -152.69) * mm});
            skLineSegment(sketch, "E1050", {"start": v(51, -152.69) * mm, "end": v(51.02, -152.3) * mm});
            skLineSegment(sketch, "E1051", {"start": v(51.02, -152.3) * mm, "end": v(51.1, -152.02) * mm});
            skLineSegment(sketch, "E1052", {"start": v(51.1, -152.02) * mm, "end": v(51.21, -151.85) * mm});
            skLineSegment(sketch, "E1053", {"start": v(51.21, -151.85) * mm, "end": v(51.36, -151.79) * mm});
            skLineSegment(sketch, "E1054", {"start": v(51.36, -151.79) * mm, "end": v(51.48, -151.84) * mm});
            skLineSegment(sketch, "E1055", {"start": v(51.48, -151.84) * mm, "end": v(51.56, -151.99) * mm});
            skLineSegment(sketch, "E1056", {"start": v(51.56, -151.99) * mm, "end": v(51.6, -152.56) * mm});
            skLineSegment(sketch, "E1057", {"start": v(51.6, -152.56) * mm, "end": v(51.6, -155.27) * mm});
            skLineSegment(sketch, "E1058", {"start": v(51.6, -155.27) * mm, "end": v(52, -155.27) * mm});
            skLineSegment(sketch, "E1059", {"start": v(52, -155.27) * mm, "end": v(52, -152.6) * mm});
            skLineSegment(sketch, "E1060", {"start": v(52, -152.6) * mm, "end": v(51.98, -152.04) * mm});
            skLineSegment(sketch, "E1061", {"start": v(51.98, -152.04) * mm, "end": v(51.9, -151.62) * mm});
            skLineSegment(sketch, "E1062", {"start": v(51.9, -151.62) * mm, "end": v(51.74, -151.36) * mm});
            skLineSegment(sketch, "E1063", {"start": v(51.74, -151.36) * mm, "end": v(51.49, -151.27) * mm});
            skLineSegment(sketch, "E1064", {"start": v(51.49, -151.27) * mm, "end": v(51.2, -151.41) * mm});
            skLineSegment(sketch, "E1065", {"start": v(51.2, -151.41) * mm, "end": v(50.96, -151.83) * mm});
            skLineSegment(sketch, "E1066", {"start": v(50.96, -151.83) * mm, "end": v(50.78, -151.42) * mm});
            skLineSegment(sketch, "E1067", {"start": v(50.78, -151.42) * mm, "end": v(50.47, -151.27) * mm});
            skLineSegment(sketch, "E1068", {"start": v(50.47, -151.27) * mm, "end": v(50.2, -151.41) * mm});
            skLineSegment(sketch, "E1069", {"start": v(50.2, -151.41) * mm, "end": v(50, -151.81) * mm});
            skLineSegment(sketch, "E1070", {"start": v(50, -151.81) * mm, "end": v(50, -151.4) * mm});
            skLineSegment(sketch, "E1071", {"start": v(50, -151.4) * mm, "end": v(49.62, -151.4) * mm});
            skLineSegment(sketch, "E1072", {"start": v(49.62, -151.4) * mm, "end": v(49.62, -155.27) * mm});
            skLineSegment(sketch, "E1073", {"start": v(53.07, -155.27) * mm, "end": v(53.47, -155.27) * mm});
            skLineSegment(sketch, "E1074", {"start": v(53.47, -155.27) * mm, "end": v(53.47, -152.69) * mm});
            skLineSegment(sketch, "E1075", {"start": v(53.47, -152.69) * mm, "end": v(53.5, -152.3) * mm});
            skLineSegment(sketch, "E1076", {"start": v(53.5, -152.3) * mm, "end": v(53.57, -152.02) * mm});
            skLineSegment(sketch, "E1077", {"start": v(53.57, -152.02) * mm, "end": v(53.68, -151.85) * mm});
            skLineSegment(sketch, "E1078", {"start": v(53.68, -151.85) * mm, "end": v(53.83, -151.79) * mm});
            skLineSegment(sketch, "E1079", {"start": v(53.83, -151.79) * mm, "end": v(53.94, -151.84) * mm});
            skLineSegment(sketch, "E1080", {"start": v(53.94, -151.84) * mm, "end": v(54.02, -151.99) * mm});
            skLineSegment(sketch, "E1081", {"start": v(54.02, -151.99) * mm, "end": v(54.06, -152.23) * mm});
            skLineSegment(sketch, "E1082", {"start": v(54.06, -152.23) * mm, "end": v(54.08, -152.56) * mm});
            skLineSegment(sketch, "E1083", {"start": v(54.08, -152.56) * mm, "end": v(54.08, -155.27) * mm});
            skLineSegment(sketch, "E1084", {"start": v(54.08, -155.27) * mm, "end": v(54.45, -155.27) * mm});
            skLineSegment(sketch, "E1085", {"start": v(54.45, -155.27) * mm, "end": v(54.45, -152.69) * mm});
            skLineSegment(sketch, "E1086", {"start": v(54.45, -152.69) * mm, "end": v(54.47, -152.3) * mm});
            skLineSegment(sketch, "E1087", {"start": v(54.47, -152.3) * mm, "end": v(54.55, -152.02) * mm});
            skLineSegment(sketch, "E1088", {"start": v(54.55, -152.02) * mm, "end": v(54.66, -151.85) * mm});
            skLineSegment(sketch, "E1089", {"start": v(54.66, -151.85) * mm, "end": v(54.81, -151.79) * mm});
            skLineSegment(sketch, "E1090", {"start": v(54.81, -151.79) * mm, "end": v(54.93, -151.84) * mm});
            skLineSegment(sketch, "E1091", {"start": v(54.93, -151.84) * mm, "end": v(55, -151.99) * mm});
            skLineSegment(sketch, "E1092", {"start": v(55, -151.99) * mm, "end": v(55.06, -152.56) * mm});
            skLineSegment(sketch, "E1093", {"start": v(55.06, -152.56) * mm, "end": v(55.06, -155.27) * mm});
            skLineSegment(sketch, "E1094", {"start": v(55.06, -155.27) * mm, "end": v(55.45, -155.27) * mm});
            skLineSegment(sketch, "E1095", {"start": v(55.45, -155.27) * mm, "end": v(55.45, -152.6) * mm});
            skLineSegment(sketch, "E1096", {"start": v(55.45, -152.6) * mm, "end": v(55.43, -152.04) * mm});
            skLineSegment(sketch, "E1097", {"start": v(55.43, -152.04) * mm, "end": v(55.35, -151.62) * mm});
            skLineSegment(sketch, "E1098", {"start": v(55.35, -151.62) * mm, "end": v(55.2, -151.36) * mm});
            skLineSegment(sketch, "E1099", {"start": v(55.2, -151.36) * mm, "end": v(54.94, -151.27) * mm});
            skLineSegment(sketch, "E1100", {"start": v(54.94, -151.27) * mm, "end": v(54.64, -151.41) * mm});
            skLineSegment(sketch, "E1101", {"start": v(54.64, -151.41) * mm, "end": v(54.4, -151.83) * mm});
            skLineSegment(sketch, "E1102", {"start": v(54.4, -151.83) * mm, "end": v(54.23, -151.42) * mm});
            skLineSegment(sketch, "E1103", {"start": v(54.23, -151.42) * mm, "end": v(53.92, -151.27) * mm});
            skLineSegment(sketch, "E1104", {"start": v(53.92, -151.27) * mm, "end": v(53.64, -151.41) * mm});
            skLineSegment(sketch, "E1105", {"start": v(53.64, -151.41) * mm, "end": v(53.45, -151.81) * mm});
            skLineSegment(sketch, "E1106", {"start": v(53.45, -151.81) * mm, "end": v(53.45, -151.4) * mm});
            skLineSegment(sketch, "E1107", {"start": v(53.45, -151.4) * mm, "end": v(53.07, -151.4) * mm});
            skLineSegment(sketch, "E1108", {"start": v(53.07, -151.4) * mm, "end": v(53.07, -155.27) * mm});
            skLineSegment(sketch, "E1109", {"start": v(56.51, -155.27) * mm, "end": v(58.85, -155.27) * mm});
            skLineSegment(sketch, "E1110", {"start": v(58.85, -155.27) * mm, "end": v(58.85, -154.65) * mm});
            skLineSegment(sketch, "E1111", {"start": v(58.85, -154.65) * mm, "end": v(57, -154.65) * mm});
            skLineSegment(sketch, "E1112", {"start": v(57, -154.65) * mm, "end": v(57.1, -154.31) * mm});
            skLineSegment(sketch, "E1113", {"start": v(57.1, -154.31) * mm, "end": v(57.28, -154.03) * mm});
            skLineSegment(sketch, "E1114", {"start": v(57.28, -154.03) * mm, "end": v(57.82, -153.52) * mm});
            skLineSegment(sketch, "E1115", {"start": v(57.82, -153.52) * mm, "end": v(58.11, -153.3) * mm});
            skLineSegment(sketch, "E1116", {"start": v(58.11, -153.3) * mm, "end": v(58.44, -153) * mm});
            skLineSegment(sketch, "E1117", {"start": v(58.44, -153) * mm, "end": v(58.67, -152.64) * mm});
            skLineSegment(sketch, "E1118", {"start": v(58.67, -152.64) * mm, "end": v(58.8, -152.21) * mm});
            skLineSegment(sketch, "E1119", {"start": v(58.8, -152.21) * mm, "end": v(58.85, -151.73) * mm});
            skLineSegment(sketch, "E1120", {"start": v(58.85, -151.73) * mm, "end": v(58.76, -151.12) * mm});
            skLineSegment(sketch, "E1121", {"start": v(58.76, -151.12) * mm, "end": v(58.53, -150.65) * mm});
            skLineSegment(sketch, "E1122", {"start": v(58.53, -150.65) * mm, "end": v(58.18, -150.34) * mm});
            skLineSegment(sketch, "E1123", {"start": v(58.18, -150.34) * mm, "end": v(57.73, -150.24) * mm});
            skLineSegment(sketch, "E1124", {"start": v(57.73, -150.24) * mm, "end": v(57.26, -150.36) * mm});
            skLineSegment(sketch, "E1125", {"start": v(57.26, -150.36) * mm, "end": v(56.9, -150.7) * mm});
            skLineSegment(sketch, "E1126", {"start": v(56.9, -150.7) * mm, "end": v(56.67, -151.24) * mm});
            skLineSegment(sketch, "E1127", {"start": v(56.67, -151.24) * mm, "end": v(56.59, -151.95) * mm});
            skLineSegment(sketch, "E1128", {"start": v(56.59, -151.95) * mm, "end": v(56.59, -152.05) * mm});
            skLineSegment(sketch, "E1129", {"start": v(56.59, -152.05) * mm, "end": v(57.04, -152.05) * mm});
            skLineSegment(sketch, "E1130", {"start": v(57.04, -152.05) * mm, "end": v(57.04, -152) * mm});
            skLineSegment(sketch, "E1131", {"start": v(57.04, -152) * mm, "end": v(57.08, -151.5) * mm});
            skLineSegment(sketch, "E1132", {"start": v(57.08, -151.5) * mm, "end": v(57.21, -151.14) * mm});
            skLineSegment(sketch, "E1133", {"start": v(57.21, -151.14) * mm, "end": v(57.42, -150.91) * mm});
            skLineSegment(sketch, "E1134", {"start": v(57.42, -150.91) * mm, "end": v(57.7, -150.83) * mm});
            skLineSegment(sketch, "E1135", {"start": v(57.7, -150.83) * mm, "end": v(57.99, -150.9) * mm});
            skLineSegment(sketch, "E1136", {"start": v(57.99, -150.9) * mm, "end": v(58.2, -151.09) * mm});
            skLineSegment(sketch, "E1137", {"start": v(58.2, -151.09) * mm, "end": v(58.33, -151.37) * mm});
            skLineSegment(sketch, "E1138", {"start": v(58.33, -151.37) * mm, "end": v(58.38, -151.72) * mm});
            skLineSegment(sketch, "E1139", {"start": v(58.38, -151.72) * mm, "end": v(58.35, -152.05) * mm});
            skLineSegment(sketch, "E1140", {"start": v(58.35, -152.05) * mm, "end": v(58.26, -152.33) * mm});
            skLineSegment(sketch, "E1141", {"start": v(58.26, -152.33) * mm, "end": v(58.1, -152.58) * mm});
            skLineSegment(sketch, "E1142", {"start": v(58.1, -152.58) * mm, "end": v(57.88, -152.8) * mm});
            skLineSegment(sketch, "E1143", {"start": v(57.88, -152.8) * mm, "end": v(57.6, -153.02) * mm});
            skLineSegment(sketch, "E1144", {"start": v(57.6, -153.02) * mm, "end": v(57.11, -153.47) * mm});
            skLineSegment(sketch, "E1145", {"start": v(57.11, -153.47) * mm, "end": v(56.78, -153.95) * mm});
            skLineSegment(sketch, "E1146", {"start": v(56.78, -153.95) * mm, "end": v(56.57, -154.52) * mm});
            skLineSegment(sketch, "E1147", {"start": v(56.57, -154.52) * mm, "end": v(56.51, -155.25) * mm});
            skLineSegment(sketch, "E1148", {"start": v(56.51, -155.25) * mm, "end": v(56.51, -155.27) * mm});
            skCircle(sketch, "E1149", {"center": v(67.5, 86.44) * mm, "radius": 3.25 * mm});
            skArc(sketch, "E1150", {"start": v(-22.63, -77.44) * mm, "mid": v(-35.33, -78.64) * mm, "end": v(-44.72, -87.27) * mm});
            skArc(sketch, "E1151", {"start": v(-22.63, -77.44) * mm, "mid": v(-3.96, -79.98) * mm, "end": v(14.85, -78.94) * mm});
            skArc(sketch, "E1152", {"start": v(36.1, -90.5) * mm, "mid": v(27.42, -81.15) * mm, "end": v(14.85, -78.94) * mm});
            skLineSegment(sketch, "E1153", {"start": v(43.06, -105.98) * mm, "end": v(36.1, -90.5) * mm});
            skArc(sketch, "E1154", {"start": v(43.06, -105.98) * mm, "mid": v(56.64, -112.76) * mm, "end": v(66, -100.8) * mm});
            skArc(sketch, "E1155", {"start": v(84.4, -32.8) * mm, "mid": v(70.3, -65.48) * mm, "end": v(66, -100.8) * mm});
            skArc(sketch, "E1156", {"start": v(34.98, 141.78) * mm, "mid": v(22.43, 155.74) * mm, "end": v(6.07, 146.52) * mm});
            skArc(sketch, "E1157", {"start": v(-74.8, -89.65) * mm, "mid": v(-72.12, -62.3) * mm, "end": v(-81.93, -36.63) * mm});
            skLineSegment(sketch, "E1158", {"start": v(-77.36, -97.19) * mm, "end": v(-74.8, -89.65) * mm});
            skArc(sketch, "E1159", {"start": v(-77.36, -97.19) * mm, "mid": v(-70.84, -112.04) * mm, "end": v(-55.49, -106.84) * mm});
            skLineSegment(sketch, "E1160", {"start": v(-55.49, -106.84) * mm, "end": v(-44.72, -87.27) * mm});
            skArc(sketch, "E1161", {"start": v(-59.6, -90.9) * mm, "mid": v(-55.7, -91.51) * mm, "end": v(-52.56, -89.08) * mm});
            skArc(sketch, "E1162", {"start": v(-66.93, -83.53) * mm, "mid": v(-66.25, -87.21) * mm, "end": v(-63.2, -89.39) * mm});
            skArc(sketch, "E1163", {"start": v(-57.83, -61.4) * mm, "mid": v(-63.18, -61.1) * mm, "end": v(-65.74, -65.8) * mm});
            skArc(sketch, "E1164", {"start": v(-44.86, -75.07) * mm, "mid": v(-44.45, -71.24) * mm, "end": v(-46.87, -68.26) * mm});
            skArc(sketch, "E1165", {"start": v(63.45, -68.13) * mm, "mid": v(61.41, -62.87) * mm, "end": v(55.77, -62.86) * mm});
            skArc(sketch, "E1166", {"start": v(55.2, -89.12) * mm, "mid": v(58.85, -88.02) * mm, "end": v(60.66, -84.66) * mm});
            skArc(sketch, "E1167", {"start": v(41.56, -88.04) * mm, "mid": v(44.49, -90.72) * mm, "end": v(48.44, -90.42) * mm});
            skArc(sketch, "E1168", {"start": v(39.76, -71.72) * mm, "mid": v(37.1, -74.5) * mm, "end": v(37.2, -78.36) * mm});
            skArc(sketch, "E1169", {"start": v(29.54, 140.4) * mm, "mid": v(21.7, 151.3) * mm, "end": v(10.79, 143.47) * mm});
            skLineSegment(sketch, "E1170", {"start": v(10.79, 143.47) * mm, "end": v(10.46, 141.5) * mm});
            skArc(sketch, "E1171", {"start": v(10.46, 141.5) * mm, "mid": v(18.3, 130.58) * mm, "end": v(29.21, 138.42) * mm});
            skLineSegment(sketch, "E1172", {"start": v(29.21, 138.42) * mm, "end": v(29.54, 140.4) * mm});
            skArc(sketch, "E1173", {"start": v(39.76, -71.72) * mm, "mid": v(47.97, -67.66) * mm, "end": v(55.77, -62.86) * mm});
            skLineSegment(sketch, "E1174", {"start": v(37.2, -78.36) * mm, "end": v(41.56, -88.04) * mm});
            skArc(sketch, "E1175", {"start": v(55.2, -89.12) * mm, "mid": v(51.72, -89.28) * mm, "end": v(48.44, -90.42) * mm});
            skArc(sketch, "E1176", {"start": v(63.45, -68.13) * mm, "mid": v(61.8, -76.35) * mm, "end": v(60.66, -84.66) * mm});
            skLineSegment(sketch, "E1177", {"start": v(-44.86, -75.07) * mm, "end": v(-52.56, -89.08) * mm});
            skArc(sketch, "E1178", {"start": v(-57.83, -61.4) * mm, "mid": v(-52.46, -65.01) * mm, "end": v(-46.87, -68.26) * mm});
            skArc(sketch, "E1179", {"start": v(-66.93, -83.53) * mm, "mid": v(-65.73, -74.7) * mm, "end": v(-65.74, -65.8) * mm});
            skArc(sketch, "E1180", {"start": v(-59.6, -90.9) * mm, "mid": v(-61.34, -90) * mm, "end": v(-63.2, -89.39) * mm});
            skCircle(sketch, "E1181", {"center": v(54, -101.06) * mm, "radius": 3.25 * mm});
            skCircle(sketch, "E1182", {"center": v(-66, -101.06) * mm, "radius": 3.25 * mm});
            skCircle(sketch, "E1183", {"center": v(-67.5, -48.56) * mm, "radius": 3.25 * mm});
            skCircle(sketch, "E1184", {"center": v(67.5, -48.56) * mm, "radius": 3.25 * mm});
            skCircle(sketch, "E1185", {"center": v(-67.5, 86.44) * mm, "radius": 3.25 * mm});
            skArc(sketch, "E1186", {"start": v(-81.1, 75.71) * mm, "mid": v(-99, 19.67) * mm, "end": v(-81.93, -36.63) * mm});
            skArc(sketch, "E1187", {"start": v(-81.1, 75.71) * mm, "mid": v(-78.5, 80.93) * mm, "end": v(-77.5, 86.69) * mm});
            skArc(sketch, "E1188", {"start": v(-67.75, 96.44) * mm, "mid": v(-74.57, 93.51) * mm, "end": v(-77.5, 86.69) * mm});
            skArc(sketch, "E1189", {"start": v(-67.75, 96.44) * mm, "mid": v(-62, 97.43) * mm, "end": v(-56.77, 100.05) * mm});
            skArc(sketch, "E1190", {"start": v(56.77, 100.05) * mm, "mid": v(62, 97.43) * mm, "end": v(67.75, 96.44) * mm});
            skArc(sketch, "E1191", {"start": v(84.4, -32.8) * mm, "mid": v(98.95, 21.95) * mm, "end": v(81.1, 75.71) * mm});
            skArc(sketch, "E1192", {"start": v(77.5, 86.69) * mm, "mid": v(74.57, 93.51) * mm, "end": v(67.75, 96.44) * mm});
            skArc(sketch, "E1193", {"start": v(77.5, 86.69) * mm, "mid": v(78.5, 80.93) * mm, "end": v(81.1, 75.71) * mm});
            skLineSegment(sketch, "E1194", {"start": v(6.07, 146.52) * mm, "end": v(-0.98, 128.9) * mm});
            skArc(sketch, "E1195", {"start": v(-16.26, 116.6) * mm, "mid": v(-37.44, 110.59) * mm, "end": v(-56.77, 100.05) * mm});
            skArc(sketch, "E1196", {"start": v(-16.26, 116.6) * mm, "mid": v(-7, 120.74) * mm, "end": v(-0.98, 128.9) * mm});
            skLineSegment(sketch, "E1197", {"start": v(34.98, 141.78) * mm, "end": v(36.03, 122.83) * mm});
            skArc(sketch, "E1198", {"start": v(56.77, 100.05) * mm, "mid": v(51.77, 103.33) * mm, "end": v(46.59, 106.3) * mm});
            skArc(sketch, "E1199", {"start": v(36.03, 122.83) * mm, "mid": v(39.14, 113.18) * mm, "end": v(46.59, 106.3) * mm});
            skArc(sketch, "E1200", {"start": v(-56.39, 85.85) * mm, "mid": v(-57.33, 84.79) * mm, "end": v(-57.94, 83.5) * mm});
            skArc(sketch, "E1201", {"start": v(-64.56, 76.89) * mm, "mid": v(-60.43, 79.37) * mm, "end": v(-57.94, 83.5) * mm});
            skArc(sketch, "E1202", {"start": v(-64.56, 76.89) * mm, "mid": v(-65.85, 76.28) * mm, "end": v(-66.9, 75.33) * mm});
            skArc(sketch, "E1203", {"start": v(-66.9, 75.33) * mm, "mid": v(-87.5, 18.94) * mm, "end": v(-66.9, -37.44) * mm});
            skArc(sketch, "E1204", {"start": v(-66.9, -37.44) * mm, "mid": v(-65.85, -38.4) * mm, "end": v(-64.56, -39) * mm});
            skArc(sketch, "E1205", {"start": v(-57.94, -45.61) * mm, "mid": v(-60.43, -41.49) * mm, "end": v(-64.56, -39) * mm});
            skArc(sketch, "E1206", {"start": v(-57.94, -45.61) * mm, "mid": v(-57.33, -46.9) * mm, "end": v(-56.39, -47.97) * mm});
            skArc(sketch, "E1207", {"start": v(64.56, -39) * mm, "mid": v(65.85, -38.4) * mm, "end": v(66.9, -37.44) * mm});
            skArc(sketch, "E1208", {"start": v(-56.39, -47.97) * mm, "mid": v(0, -68.56) * mm, "end": v(56.39, -47.97) * mm});
            skArc(sketch, "E1209", {"start": v(64.56, -39) * mm, "mid": v(60.43, -41.49) * mm, "end": v(57.94, -45.61) * mm});
            skArc(sketch, "E1210", {"start": v(56.39, -47.97) * mm, "mid": v(57.33, -46.9) * mm, "end": v(57.94, -45.61) * mm});
            skArc(sketch, "E1211", {"start": v(56.39, 85.85) * mm, "mid": v(0, 106.44) * mm, "end": v(-56.39, 85.85) * mm});
            skArc(sketch, "E1212", {"start": v(57.94, 83.5) * mm, "mid": v(57.33, 84.79) * mm, "end": v(56.39, 85.85) * mm});
            skArc(sketch, "E1213", {"start": v(66.9, 75.33) * mm, "mid": v(65.85, 76.28) * mm, "end": v(64.56, 76.89) * mm});
            skArc(sketch, "E1214", {"start": v(66.9, -37.44) * mm, "mid": v(87.5, 18.94) * mm, "end": v(66.9, 75.33) * mm});
            skArc(sketch, "E1215", {"start": v(57.94, 83.5) * mm, "mid": v(60.43, 79.37) * mm, "end": v(64.56, 76.89) * mm});
            skSolve(sketch);
        }
        {
            var Q0;
            Q0=makeQuery(id+"F0.imprint","IMPRINT",FACE,{"disambiguationData":[TD([[makeQuery(id+"F0.imprint","IMPRINT",EDGE,{"derivedFrom":sQuery(id+"F0.wireOp",EDGE,"E1149")}),1.0]])]});
            extrude(context, id + "F1", {"entities" : qUnion([Q0]), "depth" : 2.9 * mm});
        }
    });
